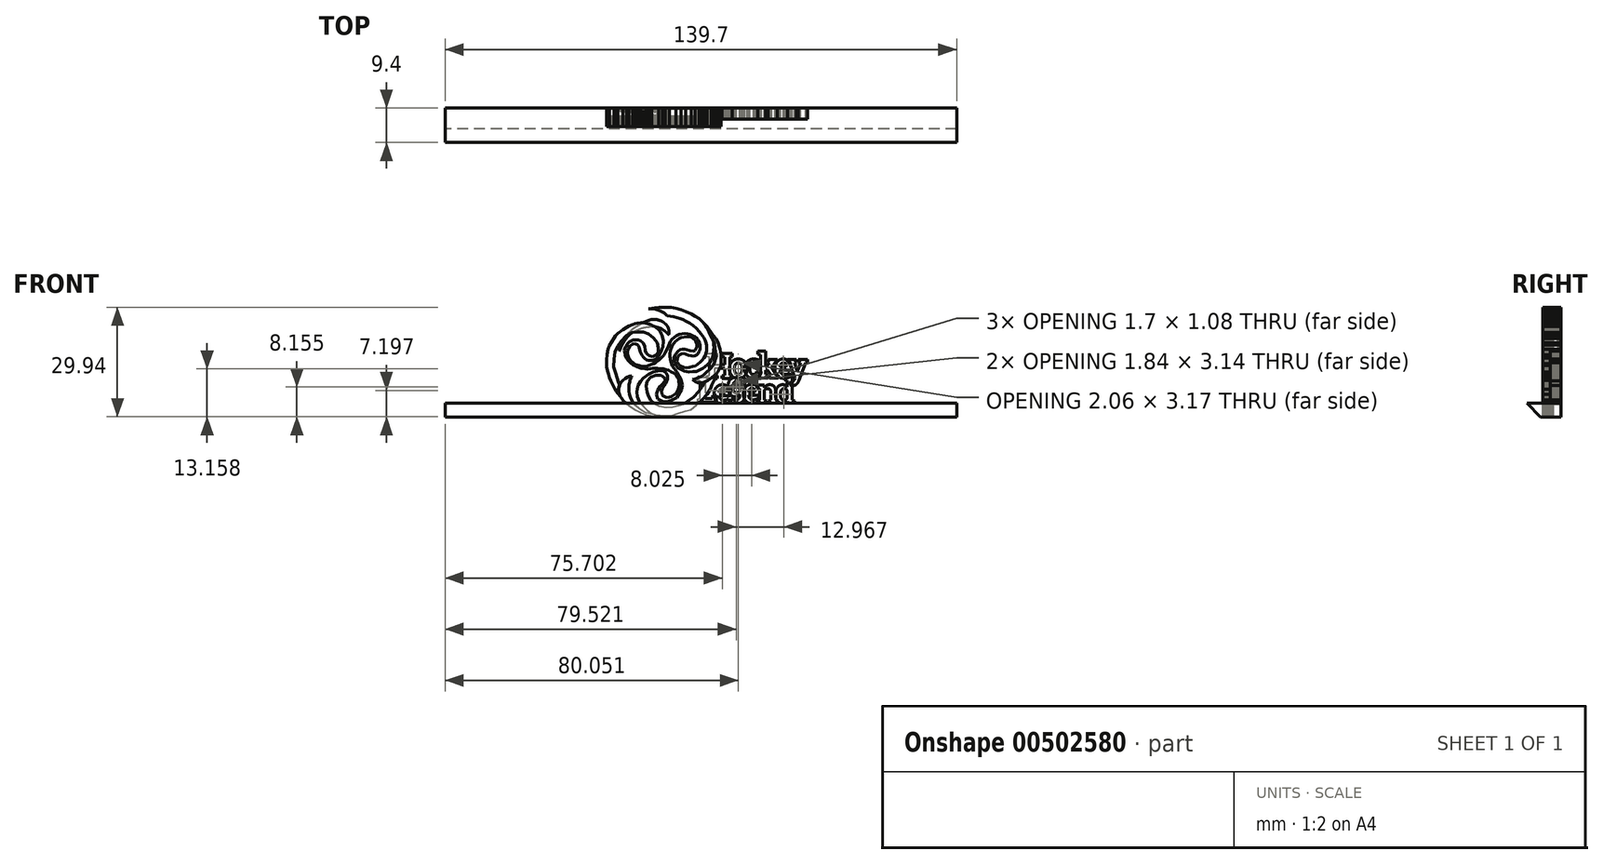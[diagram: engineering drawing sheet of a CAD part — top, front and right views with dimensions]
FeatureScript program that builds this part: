
annotation { "Feature Type Name" : "Feature", "Feature Type Description" : "" }
export const myFeature = defineFeature(function(context is Context, id is Id, definition is map)
    precondition{}
    {
        {
            var Q0;
            Q0=qCreatedBy(makeId("Front.planeOp"),FACE);
            var sketch = newSketch(context, id + "F0", { "sketchPlane" : qUnion([Q0])});
            skLineSegment(sketch, "E0", {"start": v(-33.7, 19.16) * mm, "end": v(-33.3, 20.48) * mm});
            skLineSegment(sketch, "E1", {"start": v(-33.3, 20.48) * mm, "end": v(-32.6, 22.47) * mm});
            skLineSegment(sketch, "E2", {"start": v(-32.6, 22.47) * mm, "end": v(-31.8, 23.73) * mm});
            skLineSegment(sketch, "E3", {"start": v(-31.8, 23.73) * mm, "end": v(-30.43, 25.5) * mm});
            skLineSegment(sketch, "E4", {"start": v(-30.43, 25.5) * mm, "end": v(-29.28, 26.69) * mm});
            skLineSegment(sketch, "E5", {"start": v(-29.28, 26.69) * mm, "end": v(-27.9, 27.7) * mm});
            skLineSegment(sketch, "E6", {"start": v(-27.9, 27.7) * mm, "end": v(-26.31, 28.61) * mm});
            skLineSegment(sketch, "E7", {"start": v(-26.31, 28.61) * mm, "end": v(-24.53, 29.36) * mm});
            skLineSegment(sketch, "E8", {"start": v(-24.53, 29.36) * mm, "end": v(-22.77, 30.03) * mm});
            skLineSegment(sketch, "E9", {"start": v(-20.78, 30.38) * mm, "end": v(-18.74, 30.57) * mm});
            skLineSegment(sketch, "E10", {"start": v(-18.74, 30.57) * mm, "end": v(-17.05, 30.57) * mm});
            skLineSegment(sketch, "E11", {"start": v(-17.05, 30.57) * mm, "end": v(-15.73, 30.37) * mm});
            skLineSegment(sketch, "E12", {"start": v(-15.73, 30.37) * mm, "end": v(-14.43, 30.08) * mm});
            skLineSegment(sketch, "E13", {"start": v(-14.43, 30.08) * mm, "end": v(-13.77, 29.88) * mm});
            skLineSegment(sketch, "E14", {"start": v(-13.77, 29.88) * mm, "end": v(-13.3, 29.7) * mm});
            skLineSegment(sketch, "E15", {"start": v(-13.3, 29.7) * mm, "end": v(-12.41, 29.39) * mm});
            skLineSegment(sketch, "E16", {"start": v(-12.41, 29.39) * mm, "end": v(-11.63, 29.01) * mm});
            skLineSegment(sketch, "E17", {"start": v(-11.63, 29.01) * mm, "end": v(-10.92, 28.65) * mm});
            skLineSegment(sketch, "E18", {"start": v(-10.92, 28.65) * mm, "end": v(-9.87, 28.07) * mm});
            skLineSegment(sketch, "E19", {"start": v(-9.87, 28.07) * mm, "end": v(-9.21, 27.61) * mm});
            skLineSegment(sketch, "E20", {"start": v(-9.21, 27.61) * mm, "end": v(-8.27, 26.91) * mm});
            skLineSegment(sketch, "E21", {"start": v(-8.27, 26.91) * mm, "end": v(-7.68, 26.29) * mm});
            skLineSegment(sketch, "E22", {"start": v(-7.68, 26.29) * mm, "end": v(-6.99, 25.65) * mm});
            skLineSegment(sketch, "E23", {"start": v(-6.99, 25.65) * mm, "end": v(-6.42, 25.01) * mm});
            skLineSegment(sketch, "E24", {"start": v(-6.42, 25.01) * mm, "end": v(-5.75, 24.03) * mm});
            skLineSegment(sketch, "E25", {"start": v(-5.75, 24.03) * mm, "end": v(-5.27, 23.32) * mm});
            skLineSegment(sketch, "E26", {"start": v(-5.27, 23.32) * mm, "end": v(-4.81, 22.67) * mm});
            skLineSegment(sketch, "E27", {"start": v(-4.81, 22.67) * mm, "end": v(-4.32, 21.95) * mm});
            skLineSegment(sketch, "E28", {"start": v(-4.32, 21.95) * mm, "end": v(-3.97, 21.3) * mm});
            skLineSegment(sketch, "E29", {"start": v(-3.97, 21.3) * mm, "end": v(-3.66, 20.68) * mm});
            skLineSegment(sketch, "E30", {"start": v(-3.66, 20.68) * mm, "end": v(-3.37, 19.88) * mm});
            skLineSegment(sketch, "E31", {"start": v(-3.37, 19.88) * mm, "end": v(-3.16, 19.05) * mm});
            skLineSegment(sketch, "E32", {"start": v(-3.16, 19.05) * mm, "end": v(-3, 18.35) * mm});
            skLineSegment(sketch, "E33", {"start": v(-3, 18.35) * mm, "end": v(-2.85, 17.43) * mm});
            skLineSegment(sketch, "E34", {"start": v(-2.85, 17.43) * mm, "end": v(-2.78, 16.73) * mm});
            skLineSegment(sketch, "E35", {"start": v(-2.78, 16.73) * mm, "end": v(-2.78, 15.96) * mm});
            skLineSegment(sketch, "E36", {"start": v(-2.78, 15.96) * mm, "end": v(-2.78, 15.27) * mm});
            skLineSegment(sketch, "E37", {"start": v(-2.78, 15.27) * mm, "end": v(-2.97, 14.6) * mm});
            skLineSegment(sketch, "E38", {"start": v(-2.97, 14.6) * mm, "end": v(-3.1, 14.21) * mm});
            skLineSegment(sketch, "E39", {"start": v(-3.1, 14.21) * mm, "end": v(-3.35, 13.67) * mm});
            skLineSegment(sketch, "E40", {"start": v(-3.35, 13.67) * mm, "end": v(-3.6, 13.13) * mm});
            skLineSegment(sketch, "E41", {"start": v(-3.6, 13.13) * mm, "end": v(-3.8, 12.58) * mm});
            skLineSegment(sketch, "E42", {"start": v(-3.8, 12.58) * mm, "end": v(-4.04, 11.95) * mm});
            skLineSegment(sketch, "E43", {"start": v(-4.04, 11.95) * mm, "end": v(-4.27, 11.36) * mm});
            skLineSegment(sketch, "E44", {"start": v(-4.27, 11.36) * mm, "end": v(-4.6, 10.6) * mm});
            skLineSegment(sketch, "E45", {"start": v(-4.6, 10.6) * mm, "end": v(-4.94, 9.83) * mm});
            skLineSegment(sketch, "E46", {"start": v(-4.94, 9.83) * mm, "end": v(-5.28, 9.04) * mm});
            skLineSegment(sketch, "E47", {"start": v(-5.28, 9.04) * mm, "end": v(-5.57, 8.47) * mm});
            skLineSegment(sketch, "E48", {"start": v(-5.57, 8.47) * mm, "end": v(-5.92, 7.85) * mm});
            skLineSegment(sketch, "E49", {"start": v(-5.92, 7.85) * mm, "end": v(-6.38, 7.05) * mm});
            skLineSegment(sketch, "E50", {"start": v(-6.38, 7.05) * mm, "end": v(-6.91, 6.24) * mm});
            skLineSegment(sketch, "E51", {"start": v(-6.91, 6.24) * mm, "end": v(-7.44, 5.65) * mm});
            skLineSegment(sketch, "E52", {"start": v(-7.44, 5.65) * mm, "end": v(-8.07, 5) * mm});
            skLineSegment(sketch, "E53", {"start": v(-8.07, 5) * mm, "end": v(-8.73, 4.35) * mm});
            skLineSegment(sketch, "E54", {"start": v(-8.73, 4.35) * mm, "end": v(-9.42, 3.8) * mm});
            skLineSegment(sketch, "E55", {"start": v(-9.42, 3.8) * mm, "end": v(-10.18, 3.24) * mm});
            skLineSegment(sketch, "E56", {"start": v(-10.18, 3.24) * mm, "end": v(-10.97, 2.83) * mm});
            skLineSegment(sketch, "E57", {"start": v(-10.97, 2.83) * mm, "end": v(-11.64, 2.49) * mm});
            skLineSegment(sketch, "E58", {"start": v(-11.64, 2.49) * mm, "end": v(-12.63, 2.09) * mm});
            skLineSegment(sketch, "E59", {"start": v(-12.63, 2.09) * mm, "end": v(-13.64, 1.64) * mm});
            skLineSegment(sketch, "E60", {"start": v(-13.64, 1.64) * mm, "end": v(-14.42, 1.42) * mm});
            skLineSegment(sketch, "E61", {"start": v(-14.42, 1.42) * mm, "end": v(-15.36, 1.15) * mm});
            skLineSegment(sketch, "E62", {"start": v(-15.36, 1.15) * mm, "end": v(-16.56, 0.85) * mm});
            skLineSegment(sketch, "E63", {"start": v(-16.56, 0.85) * mm, "end": v(-17.54, 0.76) * mm});
            skLineSegment(sketch, "E64", {"start": v(-17.54, 0.76) * mm, "end": v(-19.06, 0.76) * mm});
            skLineSegment(sketch, "E65", {"start": v(-19.06, 0.76) * mm, "end": v(-20.61, 0.76) * mm});
            skLineSegment(sketch, "E66", {"start": v(-20.61, 0.76) * mm, "end": v(-21.52, 0.9) * mm});
            skLineSegment(sketch, "E67", {"start": v(-21.52, 0.9) * mm, "end": v(-22.42, 1) * mm});
            skLineSegment(sketch, "E68", {"start": v(-22.42, 1) * mm, "end": v(-23.55, 1.3) * mm});
            skLineSegment(sketch, "E69", {"start": v(-23.55, 1.3) * mm, "end": v(-24.7, 1.7) * mm});
            skLineSegment(sketch, "E70", {"start": v(-24.7, 1.7) * mm, "end": v(-25.68, 2.17) * mm});
            skLineSegment(sketch, "E71", {"start": v(-25.68, 2.17) * mm, "end": v(-26.8, 2.85) * mm});
            skLineSegment(sketch, "E72", {"start": v(-26.8, 2.85) * mm, "end": v(-27.8, 3.53) * mm});
            skLineSegment(sketch, "E73", {"start": v(-27.8, 3.53) * mm, "end": v(-28.58, 4.16) * mm});
            skLineSegment(sketch, "E74", {"start": v(-28.58, 4.16) * mm, "end": v(-29.23, 4.73) * mm});
            skLineSegment(sketch, "E75", {"start": v(-29.23, 4.73) * mm, "end": v(-29.99, 5.52) * mm});
            skLineSegment(sketch, "E76", {"start": v(-29.99, 5.52) * mm, "end": v(-30.66, 6.36) * mm});
            skLineSegment(sketch, "E77", {"start": v(-30.66, 6.36) * mm, "end": v(-31.17, 7.15) * mm});
            skLineSegment(sketch, "E78", {"start": v(-31.17, 7.15) * mm, "end": v(-31.73, 7.95) * mm});
            skLineSegment(sketch, "E79", {"start": v(-31.73, 7.95) * mm, "end": v(-32.2, 8.8) * mm});
            skLineSegment(sketch, "E80", {"start": v(-32.2, 8.8) * mm, "end": v(-32.59, 9.61) * mm});
            skLineSegment(sketch, "E81", {"start": v(-32.59, 9.61) * mm, "end": v(-33.05, 10.63) * mm});
            skLineSegment(sketch, "E82", {"start": v(-33.05, 10.63) * mm, "end": v(-33.36, 11.4) * mm});
            skLineSegment(sketch, "E83", {"start": v(-33.36, 11.4) * mm, "end": v(-33.53, 11.9) * mm});
            skLineSegment(sketch, "E84", {"start": v(-33.53, 11.9) * mm, "end": v(-33.7, 12.5) * mm});
            skLineSegment(sketch, "E85", {"start": v(-33.7, 12.5) * mm, "end": v(-33.89, 13.2) * mm});
            skLineSegment(sketch, "E86", {"start": v(-33.89, 13.2) * mm, "end": v(-34.04, 14.07) * mm});
            skLineSegment(sketch, "E87", {"start": v(-34.04, 14.07) * mm, "end": v(-34.09, 14.6) * mm});
            skLineSegment(sketch, "E88", {"start": v(-34.09, 14.6) * mm, "end": v(-34.17, 15.53) * mm});
            skLineSegment(sketch, "E89", {"start": v(-34.17, 15.53) * mm, "end": v(-34.17, 16.35) * mm});
            skLineSegment(sketch, "E90", {"start": v(-34.17, 16.35) * mm, "end": v(-34.1, 17.06) * mm});
            skLineSegment(sketch, "E91", {"start": v(-34.1, 17.06) * mm, "end": v(-33.97, 17.72) * mm});
            skLineSegment(sketch, "E92", {"start": v(-33.97, 17.72) * mm, "end": v(-33.9, 18.17) * mm});
            skLineSegment(sketch, "E93", {"start": v(-33.9, 18.17) * mm, "end": v(-33.7, 19.16) * mm});
            skLineSegment(sketch, "E94", {"start": v(-33.7, 19.16) * mm, "end": v(-32.8, 21.26) * mm});
            skLineSegment(sketch, "E95", {"start": v(-32.8, 21.26) * mm, "end": v(-31.7, 23.03) * mm});
            skLineSegment(sketch, "E96", {"start": v(-31.7, 23.03) * mm, "end": v(-30.69, 24.35) * mm});
            skLineSegment(sketch, "E97", {"start": v(-30.69, 24.35) * mm, "end": v(-29.56, 25.32) * mm});
            skLineSegment(sketch, "E98", {"start": v(-29.56, 25.32) * mm, "end": v(-28.24, 26.19) * mm});
            skLineSegment(sketch, "E99", {"start": v(-28.24, 26.19) * mm, "end": v(-26, 27.12) * mm});
            skLineSegment(sketch, "E100", {"start": v(-26, 27.12) * mm, "end": v(-24.15, 27.5) * mm});
            skLineSegment(sketch, "E101", {"start": v(-24.15, 27.5) * mm, "end": v(-22.35, 27.66) * mm});
            skLineSegment(sketch, "E102", {"start": v(-22.35, 27.66) * mm, "end": v(-20.72, 27.34) * mm});
            skLineSegment(sketch, "E103", {"start": v(-20.72, 27.34) * mm, "end": v(-19.5, 26.97) * mm});
            skLineSegment(sketch, "E104", {"start": v(-19.5, 26.97) * mm, "end": v(-18.35, 26.19) * mm});
            skLineSegment(sketch, "E105", {"start": v(-18.35, 26.19) * mm, "end": v(-17.54, 25.56) * mm});
            skLineSegment(sketch, "E106", {"start": v(-17.54, 25.56) * mm, "end": v(-16.86, 24.84) * mm});
            skLineSegment(sketch, "E107", {"start": v(-16.86, 24.84) * mm, "end": v(-16.7, 25.66) * mm});
            skLineSegment(sketch, "E108", {"start": v(-16.7, 25.66) * mm, "end": v(-16.76, 26.4) * mm});
            skLineSegment(sketch, "E109", {"start": v(-16.76, 26.4) * mm, "end": v(-17, 27.17) * mm});
            skLineSegment(sketch, "E110", {"start": v(-17, 27.17) * mm, "end": v(-17.38, 27.85) * mm});
            skLineSegment(sketch, "E111", {"start": v(-17.38, 27.85) * mm, "end": v(-17.54, 28.14) * mm});
            skLineSegment(sketch, "E112", {"start": v(-17.54, 28.14) * mm, "end": v(-18.13, 28.65) * mm});
            skLineSegment(sketch, "E113", {"start": v(-18.13, 28.65) * mm, "end": v(-18.74, 29.18) * mm});
            skLineSegment(sketch, "E114", {"start": v(-18.74, 29.18) * mm, "end": v(-19.33, 29.5) * mm});
            skLineSegment(sketch, "E115", {"start": v(-19.33, 29.5) * mm, "end": v(-20.06, 29.73) * mm});
            skLineSegment(sketch, "E116", {"start": v(-20.06, 29.73) * mm, "end": v(-20.78, 29.94) * mm});
            skLineSegment(sketch, "E117", {"start": v(-20.78, 29.94) * mm, "end": v(-21.32, 30.05) * mm});
            skLineSegment(sketch, "E118", {"start": v(-21.32, 30.05) * mm, "end": v(-21.83, 30.05) * mm});
            skLineSegment(sketch, "E119", {"start": v(-21.83, 30.05) * mm, "end": v(-22.48, 30) * mm});
            skLineSegment(sketch, "E120", {"start": v(-22.48, 30) * mm, "end": v(-22.77, 30.03) * mm});
            skSolve(sketch);
        }
        {
            var Q0;
            Q0=qCreatedBy(makeId("Front.planeOp"),FACE);
            var sketch = newSketch(context, id + "F1", { "sketchPlane" : qUnion([Q0])});
            skLineSegment(sketch, "E121", {"start": v(-17.59, 28.18) * mm, "end": v(-16.68, 28.05) * mm});
            skLineSegment(sketch, "E122", {"start": v(-16.68, 28.05) * mm, "end": v(-15.74, 27.89) * mm});
            skLineSegment(sketch, "E123", {"start": v(-15.74, 27.89) * mm, "end": v(-14.88, 27.66) * mm});
            skLineSegment(sketch, "E124", {"start": v(-14.88, 27.66) * mm, "end": v(-14, 27.4) * mm});
            skLineSegment(sketch, "E125", {"start": v(-14, 27.4) * mm, "end": v(-13.3, 27.13) * mm});
            skLineSegment(sketch, "E126", {"start": v(-13.3, 27.13) * mm, "end": v(-12.35, 26.65) * mm});
            skLineSegment(sketch, "E127", {"start": v(-12.35, 26.65) * mm, "end": v(-11.37, 26.16) * mm});
            skLineSegment(sketch, "E128", {"start": v(-11.37, 26.16) * mm, "end": v(-10.4, 25.46) * mm});
            skLineSegment(sketch, "E129", {"start": v(-10.4, 25.46) * mm, "end": v(-9.57, 24.7) * mm});
            skLineSegment(sketch, "E130", {"start": v(-9.57, 24.7) * mm, "end": v(-8.82, 23.91) * mm});
            skLineSegment(sketch, "E131", {"start": v(-8.82, 23.91) * mm, "end": v(-8.25, 23.18) * mm});
            skLineSegment(sketch, "E132", {"start": v(-8.25, 23.18) * mm, "end": v(-7.58, 22.23) * mm});
            skLineSegment(sketch, "E133", {"start": v(-7.58, 22.23) * mm, "end": v(-7.2, 21.49) * mm});
            skLineSegment(sketch, "E134", {"start": v(-7.2, 21.49) * mm, "end": v(-6.86, 20.66) * mm});
            skLineSegment(sketch, "E135", {"start": v(-6.86, 20.66) * mm, "end": v(-6.73, 20.08) * mm});
            skLineSegment(sketch, "E136", {"start": v(-6.73, 20.08) * mm, "end": v(-6.73, 19.2) * mm});
            skLineSegment(sketch, "E137", {"start": v(-6.73, 19.2) * mm, "end": v(-6.78, 18.56) * mm});
            skLineSegment(sketch, "E138", {"start": v(-6.78, 18.56) * mm, "end": v(-6.98, 17.79) * mm});
            skLineSegment(sketch, "E139", {"start": v(-6.98, 17.79) * mm, "end": v(-7.2, 17.29) * mm});
            skLineSegment(sketch, "E140", {"start": v(-7.2, 17.29) * mm, "end": v(-7.52, 16.69) * mm});
            skLineSegment(sketch, "E141", {"start": v(-7.52, 16.69) * mm, "end": v(-8.02, 16.03) * mm});
            skLineSegment(sketch, "E142", {"start": v(-8.02, 16.03) * mm, "end": v(-8.55, 15.5) * mm});
            skLineSegment(sketch, "E143", {"start": v(-8.55, 15.5) * mm, "end": v(-9.17, 15.02) * mm});
            skLineSegment(sketch, "E144", {"start": v(-9.17, 15.02) * mm, "end": v(-9.81, 14.52) * mm});
            skLineSegment(sketch, "E145", {"start": v(-9.81, 14.52) * mm, "end": v(-10.54, 14.3) * mm});
            skLineSegment(sketch, "E146", {"start": v(-10.54, 14.3) * mm, "end": v(-11.44, 14.1) * mm});
            skLineSegment(sketch, "E147", {"start": v(-11.44, 14.1) * mm, "end": v(-12.2, 14) * mm});
            skLineSegment(sketch, "E148", {"start": v(-12.2, 14) * mm, "end": v(-13.06, 14.14) * mm});
            skLineSegment(sketch, "E149", {"start": v(-13.06, 14.14) * mm, "end": v(-13.88, 14.47) * mm});
            skLineSegment(sketch, "E150", {"start": v(-13.88, 14.47) * mm, "end": v(-14.41, 14.82) * mm});
            skLineSegment(sketch, "E151", {"start": v(-14.41, 14.82) * mm, "end": v(-14.66, 15.3) * mm});
            skLineSegment(sketch, "E152", {"start": v(-14.66, 15.3) * mm, "end": v(-14.86, 15.77) * mm});
            skLineSegment(sketch, "E153", {"start": v(-14.86, 15.77) * mm, "end": v(-14.8, 16.39) * mm});
            skLineSegment(sketch, "E154", {"start": v(-14.8, 16.39) * mm, "end": v(-14.65, 16.95) * mm});
            skLineSegment(sketch, "E155", {"start": v(-14.65, 16.95) * mm, "end": v(-14.14, 17.46) * mm});
            skLineSegment(sketch, "E156", {"start": v(-14.14, 17.46) * mm, "end": v(-13.66, 17.71) * mm});
            skLineSegment(sketch, "E157", {"start": v(-13.66, 17.71) * mm, "end": v(-13.04, 17.85) * mm});
            skLineSegment(sketch, "E158", {"start": v(-13.04, 17.85) * mm, "end": v(-12.42, 17.7) * mm});
            skLineSegment(sketch, "E159", {"start": v(-12.42, 17.7) * mm, "end": v(-11.69, 17.43) * mm});
            skLineSegment(sketch, "E160", {"start": v(-11.69, 17.43) * mm, "end": v(-11.01, 17.26) * mm});
            skLineSegment(sketch, "E161", {"start": v(-11.01, 17.26) * mm, "end": v(-10.44, 17.19) * mm});
            skLineSegment(sketch, "E162", {"start": v(-10.44, 17.19) * mm, "end": v(-10, 17.28) * mm});
            skLineSegment(sketch, "E163", {"start": v(-10, 17.28) * mm, "end": v(-9.5, 17.54) * mm});
            skLineSegment(sketch, "E164", {"start": v(-9.5, 17.54) * mm, "end": v(-9.1, 17.86) * mm});
            skLineSegment(sketch, "E165", {"start": v(-9.1, 17.86) * mm, "end": v(-8.9, 18.3) * mm});
            skLineSegment(sketch, "E166", {"start": v(-8.9, 18.3) * mm, "end": v(-8.72, 18.67) * mm});
            skLineSegment(sketch, "E167", {"start": v(-8.72, 18.67) * mm, "end": v(-8.6, 19.14) * mm});
            skLineSegment(sketch, "E168", {"start": v(-8.6, 19.14) * mm, "end": v(-8.6, 19.54) * mm});
            skLineSegment(sketch, "E169", {"start": v(-8.6, 19.54) * mm, "end": v(-8.6, 20.08) * mm});
            skLineSegment(sketch, "E170", {"start": v(-8.6, 20.08) * mm, "end": v(-8.73, 20.69) * mm});
            skLineSegment(sketch, "E171", {"start": v(-8.73, 20.69) * mm, "end": v(-9, 21.33) * mm});
            skLineSegment(sketch, "E172", {"start": v(-9, 21.33) * mm, "end": v(-9.2, 21.7) * mm});
            skLineSegment(sketch, "E173", {"start": v(-9.2, 21.7) * mm, "end": v(-9.48, 22.06) * mm});
            skLineSegment(sketch, "E174", {"start": v(-9.48, 22.06) * mm, "end": v(-9.97, 22.5) * mm});
            skLineSegment(sketch, "E175", {"start": v(-9.97, 22.5) * mm, "end": v(-10.54, 22.77) * mm});
            skLineSegment(sketch, "E176", {"start": v(-10.54, 22.77) * mm, "end": v(-11.33, 23.08) * mm});
            skLineSegment(sketch, "E177", {"start": v(-11.33, 23.08) * mm, "end": v(-11.96, 23.25) * mm});
            skLineSegment(sketch, "E178", {"start": v(-11.96, 23.25) * mm, "end": v(-12.7, 23.32) * mm});
            skLineSegment(sketch, "E179", {"start": v(-12.7, 23.32) * mm, "end": v(-13.51, 23.23) * mm});
            skLineSegment(sketch, "E180", {"start": v(-13.51, 23.23) * mm, "end": v(-14.27, 23.08) * mm});
            skLineSegment(sketch, "E181", {"start": v(-14.27, 23.08) * mm, "end": v(-15.04, 22.67) * mm});
            skLineSegment(sketch, "E182", {"start": v(-15.04, 22.67) * mm, "end": v(-15.57, 22.26) * mm});
            skLineSegment(sketch, "E183", {"start": v(-15.57, 22.26) * mm, "end": v(-16.16, 21.8) * mm});
            skLineSegment(sketch, "E184", {"start": v(-16.16, 21.8) * mm, "end": v(-16.62, 21.17) * mm});
            skLineSegment(sketch, "E185", {"start": v(-16.62, 21.17) * mm, "end": v(-16.97, 20.58) * mm});
            skLineSegment(sketch, "E186", {"start": v(-16.97, 20.58) * mm, "end": v(-17.24, 19.87) * mm});
            skLineSegment(sketch, "E187", {"start": v(-17.24, 19.87) * mm, "end": v(-17.63, 19.02) * mm});
            skLineSegment(sketch, "E188", {"start": v(-17.63, 19.02) * mm, "end": v(-18.02, 18.18) * mm});
            skLineSegment(sketch, "E189", {"start": v(-18.02, 18.18) * mm, "end": v(-18.47, 17.4) * mm});
            skLineSegment(sketch, "E190", {"start": v(-18.47, 17.4) * mm, "end": v(-19.07, 16.73) * mm});
            skLineSegment(sketch, "E191", {"start": v(-19.07, 16.73) * mm, "end": v(-19.8, 16.05) * mm});
            skLineSegment(sketch, "E192", {"start": v(-19.8, 16.05) * mm, "end": v(-20.62, 15.5) * mm});
            skLineSegment(sketch, "E193", {"start": v(-20.62, 15.5) * mm, "end": v(-21.3, 15.14) * mm});
            skLineSegment(sketch, "E194", {"start": v(-21.3, 15.14) * mm, "end": v(-22.02, 14.87) * mm});
            skLineSegment(sketch, "E195", {"start": v(-22.02, 14.87) * mm, "end": v(-22.85, 14.53) * mm});
            skLineSegment(sketch, "E196", {"start": v(-22.85, 14.53) * mm, "end": v(-23.59, 14.38) * mm});
            skLineSegment(sketch, "E197", {"start": v(-23.59, 14.38) * mm, "end": v(-24.4, 14.38) * mm});
            skLineSegment(sketch, "E198", {"start": v(-24.4, 14.38) * mm, "end": v(-25.23, 14.53) * mm});
            skLineSegment(sketch, "E199", {"start": v(-25.23, 14.53) * mm, "end": v(-26.19, 14.9) * mm});
            skLineSegment(sketch, "E200", {"start": v(-26.19, 14.9) * mm, "end": v(-26.89, 15.3) * mm});
            skLineSegment(sketch, "E201", {"start": v(-26.89, 15.3) * mm, "end": v(-27.37, 15.75) * mm});
            skLineSegment(sketch, "E202", {"start": v(-27.37, 15.75) * mm, "end": v(-27.81, 16.32) * mm});
            skLineSegment(sketch, "E203", {"start": v(-27.81, 16.32) * mm, "end": v(-28.1, 16.87) * mm});
            skLineSegment(sketch, "E204", {"start": v(-28.1, 16.87) * mm, "end": v(-28.31, 17.7) * mm});
            skLineSegment(sketch, "E205", {"start": v(-28.31, 17.7) * mm, "end": v(-28.31, 18.37) * mm});
            skLineSegment(sketch, "E206", {"start": v(-28.31, 18.37) * mm, "end": v(-28.21, 18.94) * mm});
            skLineSegment(sketch, "E207", {"start": v(-28.21, 18.94) * mm, "end": v(-28.1, 19.34) * mm});
            skLineSegment(sketch, "E208", {"start": v(-28.1, 19.34) * mm, "end": v(-27.77, 19.9) * mm});
            skLineSegment(sketch, "E209", {"start": v(-27.77, 19.9) * mm, "end": v(-27.4, 20.24) * mm});
            skLineSegment(sketch, "E210", {"start": v(-27.4, 20.24) * mm, "end": v(-26.9, 20.48) * mm});
            skLineSegment(sketch, "E211", {"start": v(-26.9, 20.48) * mm, "end": v(-26.35, 20.53) * mm});
            skLineSegment(sketch, "E212", {"start": v(-26.35, 20.53) * mm, "end": v(-26.08, 20.47) * mm});
            skLineSegment(sketch, "E213", {"start": v(-26.08, 20.47) * mm, "end": v(-25.65, 20.3) * mm});
            skLineSegment(sketch, "E214", {"start": v(-25.65, 20.3) * mm, "end": v(-25.4, 20.02) * mm});
            skLineSegment(sketch, "E215", {"start": v(-25.4, 20.02) * mm, "end": v(-25.24, 19.53) * mm});
            skLineSegment(sketch, "E216", {"start": v(-25.24, 19.53) * mm, "end": v(-24.88, 18.41) * mm});
            skLineSegment(sketch, "E217", {"start": v(-24.88, 18.41) * mm, "end": v(-24.66, 17.85) * mm});
            skLineSegment(sketch, "E218", {"start": v(-24.66, 17.85) * mm, "end": v(-24.4, 17.37) * mm});
            skLineSegment(sketch, "E219", {"start": v(-24.4, 17.37) * mm, "end": v(-24.07, 16.93) * mm});
            skLineSegment(sketch, "E220", {"start": v(-24.07, 16.93) * mm, "end": v(-23.62, 16.44) * mm});
            skLineSegment(sketch, "E221", {"start": v(-23.62, 16.44) * mm, "end": v(-23.12, 16.15) * mm});
            skLineSegment(sketch, "E222", {"start": v(-23.12, 16.15) * mm, "end": v(-22.6, 16.01) * mm});
            skLineSegment(sketch, "E223", {"start": v(-22.6, 16.01) * mm, "end": v(-22.12, 15.93) * mm});
            skLineSegment(sketch, "E224", {"start": v(-22.12, 15.93) * mm, "end": v(-21.5, 16.01) * mm});
            skLineSegment(sketch, "E225", {"start": v(-21.5, 16.01) * mm, "end": v(-21.12, 16.12) * mm});
            skLineSegment(sketch, "E226", {"start": v(-21.12, 16.12) * mm, "end": v(-20.65, 16.37) * mm});
            skLineSegment(sketch, "E227", {"start": v(-20.65, 16.37) * mm, "end": v(-20.16, 16.83) * mm});
            skLineSegment(sketch, "E228", {"start": v(-20.16, 16.83) * mm, "end": v(-19.85, 17.1) * mm});
            skLineSegment(sketch, "E229", {"start": v(-19.85, 17.1) * mm, "end": v(-19.6, 17.6) * mm});
            skLineSegment(sketch, "E230", {"start": v(-19.6, 17.6) * mm, "end": v(-19.35, 18.1) * mm});
            skLineSegment(sketch, "E231", {"start": v(-19.35, 18.1) * mm, "end": v(-19.03, 18.64) * mm});
            skLineSegment(sketch, "E232", {"start": v(-19.03, 18.64) * mm, "end": v(-18.91, 19.23) * mm});
            skLineSegment(sketch, "E233", {"start": v(-18.91, 19.23) * mm, "end": v(-18.77, 19.65) * mm});
            skLineSegment(sketch, "E234", {"start": v(-18.77, 19.65) * mm, "end": v(-18.67, 20.1) * mm});
            skLineSegment(sketch, "E235", {"start": v(-18.67, 20.1) * mm, "end": v(-18.62, 20.77) * mm});
            skLineSegment(sketch, "E236", {"start": v(-18.62, 20.77) * mm, "end": v(-18.62, 21.3) * mm});
            skLineSegment(sketch, "E237", {"start": v(-18.62, 21.3) * mm, "end": v(-18.68, 21.91) * mm});
            skLineSegment(sketch, "E238", {"start": v(-18.68, 21.91) * mm, "end": v(-18.97, 22.9) * mm});
            skLineSegment(sketch, "E239", {"start": v(-18.97, 22.9) * mm, "end": v(-19.2, 23.37) * mm});
            skLineSegment(sketch, "E240", {"start": v(-19.2, 23.37) * mm, "end": v(-19.4, 23.74) * mm});
            skLineSegment(sketch, "E241", {"start": v(-19.4, 23.74) * mm, "end": v(-19.88, 24.36) * mm});
            skLineSegment(sketch, "E242", {"start": v(-19.88, 24.36) * mm, "end": v(-20.56, 24.97) * mm});
            skLineSegment(sketch, "E243", {"start": v(-20.56, 24.97) * mm, "end": v(-21.04, 25.24) * mm});
            skLineSegment(sketch, "E244", {"start": v(-21.04, 25.24) * mm, "end": v(-21.38, 25.44) * mm});
            skLineSegment(sketch, "E245", {"start": v(-21.38, 25.44) * mm, "end": v(-22.12, 25.85) * mm});
            skLineSegment(sketch, "E246", {"start": v(-22.12, 25.85) * mm, "end": v(-22.57, 25.95) * mm});
            skLineSegment(sketch, "E247", {"start": v(-22.57, 25.95) * mm, "end": v(-23.45, 26.18) * mm});
            skLineSegment(sketch, "E248", {"start": v(-23.45, 26.18) * mm, "end": v(-24.1, 26.3) * mm});
            skLineSegment(sketch, "E249", {"start": v(-24.1, 26.3) * mm, "end": v(-24.77, 26.26) * mm});
            skLineSegment(sketch, "E250", {"start": v(-24.77, 26.26) * mm, "end": v(-25.66, 26.17) * mm});
            skLineSegment(sketch, "E251", {"start": v(-25.66, 26.17) * mm, "end": v(-26.27, 25.98) * mm});
            skLineSegment(sketch, "E252", {"start": v(-26.27, 25.98) * mm, "end": v(-26.98, 25.74) * mm});
            skLineSegment(sketch, "E253", {"start": v(-26.98, 25.74) * mm, "end": v(-27.95, 25.34) * mm});
            skLineSegment(sketch, "E254", {"start": v(-27.95, 25.34) * mm, "end": v(-28.58, 25.07) * mm});
            skLineSegment(sketch, "E255", {"start": v(-28.58, 25.07) * mm, "end": v(-29.6, 24.43) * mm});
            skLineSegment(sketch, "E256", {"start": v(-29.6, 24.43) * mm, "end": v(-30.3, 23.9) * mm});
            skLineSegment(sketch, "E257", {"start": v(-30.3, 23.9) * mm, "end": v(-31.05, 23.3) * mm});
            skLineSegment(sketch, "E258", {"start": v(-31.05, 23.3) * mm, "end": v(-31.6, 22.7) * mm});
            skLineSegment(sketch, "E259", {"start": v(-31.6, 22.7) * mm, "end": v(-32.06, 22.14) * mm});
            skLineSegment(sketch, "E260", {"start": v(-32.06, 22.14) * mm, "end": v(-33.26, 20.08) * mm});
            skLineSegment(sketch, "E261", {"start": v(-33.26, 20.08) * mm, "end": v(-33.7, 19.08) * mm});
            skLineSegment(sketch, "E262", {"start": v(-33.7, 19.08) * mm, "end": v(-33.95, 17.68) * mm});
            skLineSegment(sketch, "E263", {"start": v(-33.95, 17.68) * mm, "end": v(-34.13, 16.12) * mm});
            skLineSegment(sketch, "E264", {"start": v(-34.13, 16.12) * mm, "end": v(-34.13, 15.34) * mm});
            skLineSegment(sketch, "E265", {"start": v(-34.13, 15.34) * mm, "end": v(-34.04, 14.24) * mm});
            skLineSegment(sketch, "E266", {"start": v(-34.04, 14.24) * mm, "end": v(-33.83, 13.12) * mm});
            skLineSegment(sketch, "E267", {"start": v(-33.83, 13.12) * mm, "end": v(-33.6, 12.35) * mm});
            skLineSegment(sketch, "E268", {"start": v(-33.6, 12.35) * mm, "end": v(-33.3, 11.34) * mm});
            skLineSegment(sketch, "E269", {"start": v(-33.3, 11.34) * mm, "end": v(-32.93, 10.45) * mm});
            skLineSegment(sketch, "E270", {"start": v(-32.93, 10.45) * mm, "end": v(-32.6, 9.62) * mm});
            skLineSegment(sketch, "E271", {"start": v(-32.6, 9.62) * mm, "end": v(-32.3, 9.05) * mm});
            skLineSegment(sketch, "E272", {"start": v(-32.3, 9.05) * mm, "end": v(-31.54, 7.63) * mm});
            skLineSegment(sketch, "E273", {"start": v(-31.54, 7.63) * mm, "end": v(-30.98, 6.91) * mm});
            skLineSegment(sketch, "E274", {"start": v(-30.98, 6.91) * mm, "end": v(-30.4, 6.16) * mm});
            skLineSegment(sketch, "E275", {"start": v(-30.4, 6.16) * mm, "end": v(-30.82, 7.32) * mm});
            skLineSegment(sketch, "E276", {"start": v(-30.82, 7.32) * mm, "end": v(-30.82, 8.38) * mm});
            skLineSegment(sketch, "E277", {"start": v(-30.82, 8.38) * mm, "end": v(-30.56, 9.17) * mm});
            skLineSegment(sketch, "E278", {"start": v(-30.56, 9.17) * mm, "end": v(-30.96, 10.11) * mm});
            skLineSegment(sketch, "E279", {"start": v(-30.96, 10.11) * mm, "end": v(-31.54, 12.36) * mm});
            skLineSegment(sketch, "E280", {"start": v(-31.54, 12.36) * mm, "end": v(-32.14, 14.24) * mm});
            skLineSegment(sketch, "E281", {"start": v(-32.14, 14.24) * mm, "end": v(-32.1, 16.32) * mm});
            skLineSegment(sketch, "E282", {"start": v(-32.1, 16.32) * mm, "end": v(-31.74, 18.22) * mm});
            skLineSegment(sketch, "E283", {"start": v(-31.74, 18.22) * mm, "end": v(-30.97, 19.9) * mm});
            skLineSegment(sketch, "E284", {"start": v(-30.97, 19.9) * mm, "end": v(-30.14, 21.16) * mm});
            skLineSegment(sketch, "E285", {"start": v(-30.14, 21.16) * mm, "end": v(-28.8, 22.68) * mm});
            skLineSegment(sketch, "E286", {"start": v(-28.8, 22.68) * mm, "end": v(-27.04, 23.61) * mm});
            skLineSegment(sketch, "E287", {"start": v(-27.04, 23.61) * mm, "end": v(-25.72, 23.77) * mm});
            skLineSegment(sketch, "E288", {"start": v(-25.72, 23.77) * mm, "end": v(-23.98, 23.74) * mm});
            skLineSegment(sketch, "E289", {"start": v(-23.98, 23.74) * mm, "end": v(-22.6, 23.24) * mm});
            skLineSegment(sketch, "E290", {"start": v(-22.6, 23.24) * mm, "end": v(-21.28, 22.09) * mm});
            skLineSegment(sketch, "E291", {"start": v(-21.28, 22.09) * mm, "end": v(-20.24, 20.84) * mm});
            skLineSegment(sketch, "E292", {"start": v(-20.24, 20.84) * mm, "end": v(-19.95, 19.4) * mm});
            skLineSegment(sketch, "E293", {"start": v(-19.95, 19.4) * mm, "end": v(-20, 18.33) * mm});
            skLineSegment(sketch, "E294", {"start": v(-20, 18.33) * mm, "end": v(-20.5, 17.46) * mm});
            skLineSegment(sketch, "E295", {"start": v(-20.5, 17.46) * mm, "end": v(-21.55, 17.02) * mm});
            skLineSegment(sketch, "E296", {"start": v(-23.33, 18) * mm, "end": v(-23.54, 18.65) * mm});
            skLineSegment(sketch, "E297", {"start": v(-23.54, 18.65) * mm, "end": v(-23.67, 19.87) * mm});
            skLineSegment(sketch, "E298", {"start": v(-23.67, 19.87) * mm, "end": v(-24.2, 20.77) * mm});
            skLineSegment(sketch, "E299", {"start": v(-24.2, 20.77) * mm, "end": v(-24.84, 21.36) * mm});
            skLineSegment(sketch, "E300", {"start": v(-24.84, 21.36) * mm, "end": v(-25.5, 21.58) * mm});
            skLineSegment(sketch, "E301", {"start": v(-25.5, 21.58) * mm, "end": v(-26.81, 21.58) * mm});
            skLineSegment(sketch, "E302", {"start": v(-26.81, 21.58) * mm, "end": v(-27.81, 21.05) * mm});
            skLineSegment(sketch, "E303", {"start": v(-27.81, 21.05) * mm, "end": v(-28.43, 20.6) * mm});
            skLineSegment(sketch, "E304", {"start": v(-28.43, 20.6) * mm, "end": v(-28.92, 19.86) * mm});
            skLineSegment(sketch, "E305", {"start": v(-28.92, 19.86) * mm, "end": v(-29.16, 19.25) * mm});
            skLineSegment(sketch, "E306", {"start": v(-29.16, 19.25) * mm, "end": v(-29.2, 18.6) * mm});
            skLineSegment(sketch, "E307", {"start": v(-29.2, 18.6) * mm, "end": v(-29.05, 17.77) * mm});
            skLineSegment(sketch, "E308", {"start": v(-29.05, 17.77) * mm, "end": v(-28.96, 17.26) * mm});
            skLineSegment(sketch, "E309", {"start": v(-28.96, 17.26) * mm, "end": v(-28.6, 16.5) * mm});
            skLineSegment(sketch, "E310", {"start": v(-28.6, 16.5) * mm, "end": v(-28.12, 15.82) * mm});
            skLineSegment(sketch, "E311", {"start": v(-28.12, 15.82) * mm, "end": v(-27.66, 15.3) * mm});
            skLineSegment(sketch, "E312", {"start": v(-27.66, 15.3) * mm, "end": v(-26.86, 14.78) * mm});
            skLineSegment(sketch, "E313", {"start": v(-26.86, 14.78) * mm, "end": v(-26.24, 14.45) * mm});
            skLineSegment(sketch, "E314", {"start": v(-26.24, 14.45) * mm, "end": v(-25.65, 14.22) * mm});
            skLineSegment(sketch, "E315", {"start": v(-25.65, 14.22) * mm, "end": v(-24.73, 13.86) * mm});
            skLineSegment(sketch, "E316", {"start": v(-24.73, 13.86) * mm, "end": v(-23.5, 13.7) * mm});
            skLineSegment(sketch, "E317", {"start": v(-23.5, 13.7) * mm, "end": v(-22.86, 13.62) * mm});
            skLineSegment(sketch, "E318", {"start": v(-22.86, 13.62) * mm, "end": v(-22.18, 13.7) * mm});
            skLineSegment(sketch, "E319", {"start": v(-22.18, 13.7) * mm, "end": v(-21.5, 13.78) * mm});
            skLineSegment(sketch, "E320", {"start": v(-21.5, 13.78) * mm, "end": v(-21, 13.84) * mm});
            skLineSegment(sketch, "E321", {"start": v(-21, 13.84) * mm, "end": v(-20.09, 13.78) * mm});
            skLineSegment(sketch, "E322", {"start": v(-20.09, 13.78) * mm, "end": v(-19.35, 13.74) * mm});
            skLineSegment(sketch, "E323", {"start": v(-19.35, 13.74) * mm, "end": v(-18.6, 13.67) * mm});
            skLineSegment(sketch, "E324", {"start": v(-18.6, 13.67) * mm, "end": v(-17.87, 13.46) * mm});
            skLineSegment(sketch, "E325", {"start": v(-17.87, 13.46) * mm, "end": v(-17.18, 13.26) * mm});
            skLineSegment(sketch, "E326", {"start": v(-17.18, 13.26) * mm, "end": v(-16.4, 12.82) * mm});
            skLineSegment(sketch, "E327", {"start": v(-16.4, 12.82) * mm, "end": v(-15.76, 12.5) * mm});
            skLineSegment(sketch, "E328", {"start": v(-15.76, 12.5) * mm, "end": v(-15.1, 12.02) * mm});
            skLineSegment(sketch, "E329", {"start": v(-15.1, 12.02) * mm, "end": v(-14.75, 11.35) * mm});
            skLineSegment(sketch, "E330", {"start": v(-14.75, 11.35) * mm, "end": v(-14.46, 10.8) * mm});
            skLineSegment(sketch, "E331", {"start": v(-14.46, 10.8) * mm, "end": v(-14.36, 10.11) * mm});
            skLineSegment(sketch, "E332", {"start": v(-14.36, 10.11) * mm, "end": v(-14.32, 9.62) * mm});
            skLineSegment(sketch, "E333", {"start": v(-14.32, 9.62) * mm, "end": v(-14.33, 9.1) * mm});
            skLineSegment(sketch, "E334", {"start": v(-14.33, 9.1) * mm, "end": v(-14.41, 8.57) * mm});
            skLineSegment(sketch, "E335", {"start": v(-14.41, 8.57) * mm, "end": v(-14.55, 8.18) * mm});
            skLineSegment(sketch, "E336", {"start": v(-14.55, 8.18) * mm, "end": v(-14.76, 7.63) * mm});
            skLineSegment(sketch, "E337", {"start": v(-14.76, 7.63) * mm, "end": v(-14.91, 7.37) * mm});
            skLineSegment(sketch, "E338", {"start": v(-14.91, 7.37) * mm, "end": v(-15.27, 6.9) * mm});
            skLineSegment(sketch, "E339", {"start": v(-15.27, 6.9) * mm, "end": v(-15.72, 6.54) * mm});
            skLineSegment(sketch, "E340", {"start": v(-15.72, 6.54) * mm, "end": v(-16.37, 6.11) * mm});
            skLineSegment(sketch, "E341", {"start": v(-16.37, 6.11) * mm, "end": v(-16.98, 5.96) * mm});
            skLineSegment(sketch, "E342", {"start": v(-16.98, 5.96) * mm, "end": v(-17.46, 5.89) * mm});
            skLineSegment(sketch, "E343", {"start": v(-17.46, 5.89) * mm, "end": v(-18, 5.98) * mm});
            skLineSegment(sketch, "E344", {"start": v(-18, 5.98) * mm, "end": v(-18, 5.98) * mm});
            skLineSegment(sketch, "E345", {"start": v(-18, 5.98) * mm, "end": v(-18.68, 6.36) * mm});
            skLineSegment(sketch, "E346", {"start": v(-18.68, 6.36) * mm, "end": v(-19, 6.7) * mm});
            skLineSegment(sketch, "E347", {"start": v(-19, 6.7) * mm, "end": v(-19.08, 7.3) * mm});
            skLineSegment(sketch, "E348", {"start": v(-19.08, 7.3) * mm, "end": v(-19.13, 7.63) * mm});
            skLineSegment(sketch, "E349", {"start": v(-19.13, 7.63) * mm, "end": v(-18.85, 8.36) * mm});
            skLineSegment(sketch, "E350", {"start": v(-18.85, 8.36) * mm, "end": v(-18, 9.58) * mm});
            skLineSegment(sketch, "E351", {"start": v(-18, 9.58) * mm, "end": v(-18, 9.6) * mm});
            skLineSegment(sketch, "E352", {"start": v(-18, 9.6) * mm, "end": v(-17.5, 10.86) * mm});
            skLineSegment(sketch, "E353", {"start": v(-17.5, 10.86) * mm, "end": v(-17.47, 11.77) * mm});
            skLineSegment(sketch, "E354", {"start": v(-17.47, 11.77) * mm, "end": v(-17.82, 12.62) * mm});
            skLineSegment(sketch, "E355", {"start": v(-17.82, 12.62) * mm, "end": v(-18.76, 13.15) * mm});
            skLineSegment(sketch, "E356", {"start": v(-18.76, 13.15) * mm, "end": v(-20.27, 13.05) * mm});
            skLineSegment(sketch, "E357", {"start": v(-20.27, 13.05) * mm, "end": v(-21.36, 12.86) * mm});
            skLineSegment(sketch, "E358", {"start": v(-21.36, 12.86) * mm, "end": v(-22.64, 12.24) * mm});
            skLineSegment(sketch, "E359", {"start": v(-22.64, 12.24) * mm, "end": v(-24.04, 11.21) * mm});
            skLineSegment(sketch, "E360", {"start": v(-24.04, 11.21) * mm, "end": v(-24.86, 10.31) * mm});
            skLineSegment(sketch, "E361", {"start": v(-24.86, 10.31) * mm, "end": v(-25.41, 9.2) * mm});
            skLineSegment(sketch, "E362", {"start": v(-25.41, 9.2) * mm, "end": v(-25.66, 8.25) * mm});
            skLineSegment(sketch, "E363", {"start": v(-25.66, 8.25) * mm, "end": v(-25.8, 7.3) * mm});
            skLineSegment(sketch, "E364", {"start": v(-25.8, 7.3) * mm, "end": v(-25.73, 6.09) * mm});
            skLineSegment(sketch, "E365", {"start": v(-25.73, 6.09) * mm, "end": v(-25.16, 4.78) * mm});
            skLineSegment(sketch, "E366", {"start": v(-25.16, 4.78) * mm, "end": v(-24.07, 3.4) * mm});
            skLineSegment(sketch, "E367", {"start": v(-24.07, 3.4) * mm, "end": v(-23.05, 2.4) * mm});
            skLineSegment(sketch, "E368", {"start": v(-23.05, 2.4) * mm, "end": v(-21.87, 1.52) * mm});
            skLineSegment(sketch, "E369", {"start": v(-21.87, 1.52) * mm, "end": v(-20.68, 1.14) * mm});
            skLineSegment(sketch, "E370", {"start": v(-20.68, 1.14) * mm, "end": v(-19.55, 0.9) * mm});
            skLineSegment(sketch, "E371", {"start": v(-19.55, 0.9) * mm, "end": v(-18.27, 0.83) * mm});
            skLineSegment(sketch, "E372", {"start": v(-18.27, 0.83) * mm, "end": v(-16.45, 0.9) * mm});
            skLineSegment(sketch, "E373", {"start": v(-16.45, 0.9) * mm, "end": v(-14.64, 1.49) * mm});
            skLineSegment(sketch, "E374", {"start": v(-14.64, 1.49) * mm, "end": v(-12.6, 2.12) * mm});
            skLineSegment(sketch, "E375", {"start": v(-12.6, 2.12) * mm, "end": v(-11.1, 2.55) * mm});
            skLineSegment(sketch, "E376", {"start": v(-11.1, 2.55) * mm, "end": v(-9.55, 3.82) * mm});
            skLineSegment(sketch, "E377", {"start": v(-9.55, 3.82) * mm, "end": v(-8.04, 5.22) * mm});
            skLineSegment(sketch, "E378", {"start": v(-8.04, 5.22) * mm, "end": v(-6.68, 6.77) * mm});
            skLineSegment(sketch, "E379", {"start": v(-6.68, 6.77) * mm, "end": v(-5.8, 8.1) * mm});
            skLineSegment(sketch, "E380", {"start": v(-5.8, 8.1) * mm, "end": v(-5.33, 9.25) * mm});
            skLineSegment(sketch, "E381", {"start": v(-5.33, 9.25) * mm, "end": v(-4.8, 10.52) * mm});
            skLineSegment(sketch, "E382", {"start": v(-4.8, 10.52) * mm, "end": v(-4.29, 11.36) * mm});
            skLineSegment(sketch, "E383", {"start": v(-4.29, 11.36) * mm, "end": v(-4.07, 12.3) * mm});
            skLineSegment(sketch, "E384", {"start": v(-4.07, 12.3) * mm, "end": v(-5.89, 10.9) * mm});
            skLineSegment(sketch, "E385", {"start": v(-5.89, 10.9) * mm, "end": v(-7.46, 9.91) * mm});
            skLineSegment(sketch, "E386", {"start": v(-7.46, 9.91) * mm, "end": v(-8.08, 8.8) * mm});
            skLineSegment(sketch, "E387", {"start": v(-8.08, 8.8) * mm, "end": v(-8.96, 7.49) * mm});
            skLineSegment(sketch, "E388", {"start": v(-8.96, 7.49) * mm, "end": v(-10.36, 5.96) * mm});
            skLineSegment(sketch, "E389", {"start": v(-10.36, 5.96) * mm, "end": v(-11.94, 4.77) * mm});
            skLineSegment(sketch, "E390", {"start": v(-11.94, 4.77) * mm, "end": v(-13.13, 3.98) * mm});
            skLineSegment(sketch, "E391", {"start": v(-13.13, 3.98) * mm, "end": v(-14.55, 3.49) * mm});
            skLineSegment(sketch, "E392", {"start": v(-14.55, 3.49) * mm, "end": v(-16.1, 3.18) * mm});
            skLineSegment(sketch, "E393", {"start": v(-16.1, 3.18) * mm, "end": v(-17.85, 3) * mm});
            skLineSegment(sketch, "E394", {"start": v(-17.85, 3) * mm, "end": v(-19.77, 3.44) * mm});
            skLineSegment(sketch, "E395", {"start": v(-19.77, 3.44) * mm, "end": v(-21, 4.07) * mm});
            skLineSegment(sketch, "E396", {"start": v(-21, 4.07) * mm, "end": v(-22, 5.1) * mm});
            skLineSegment(sketch, "E397", {"start": v(-22, 5.1) * mm, "end": v(-22.6, 6.18) * mm});
            skLineSegment(sketch, "E398", {"start": v(-22.6, 6.18) * mm, "end": v(-23.07, 7.3) * mm});
            skLineSegment(sketch, "E399", {"start": v(-23.07, 7.3) * mm, "end": v(-23.26, 9.07) * mm});
            skLineSegment(sketch, "E400", {"start": v(-23.26, 9.07) * mm, "end": v(-22.97, 10.27) * mm});
            skLineSegment(sketch, "E401", {"start": v(-22.97, 10.27) * mm, "end": v(-22.04, 11.44) * mm});
            skLineSegment(sketch, "E402", {"start": v(-22.04, 11.44) * mm, "end": v(-20.58, 11.91) * mm});
            skLineSegment(sketch, "E403", {"start": v(-20.58, 11.91) * mm, "end": v(-19.19, 11.97) * mm});
            skLineSegment(sketch, "E404", {"start": v(-19.19, 11.97) * mm, "end": v(-18.16, 11.17) * mm});
            skLineSegment(sketch, "E405", {"start": v(-18.16, 11.17) * mm, "end": v(-18.14, 10.52) * mm});
            skLineSegment(sketch, "E406", {"start": v(-18.14, 10.52) * mm, "end": v(-18.71, 9.66) * mm});
            skLineSegment(sketch, "E407", {"start": v(-18.71, 9.66) * mm, "end": v(-19.47, 8.87) * mm});
            skLineSegment(sketch, "E408", {"start": v(-19.47, 8.87) * mm, "end": v(-20.18, 7.92) * mm});
            skLineSegment(sketch, "E409", {"start": v(-20.18, 7.92) * mm, "end": v(-20.45, 6.66) * mm});
            skLineSegment(sketch, "E410", {"start": v(-20.45, 6.66) * mm, "end": v(-20.15, 5.48) * mm});
            skLineSegment(sketch, "E411", {"start": v(-20.15, 5.48) * mm, "end": v(-18.9, 4.8) * mm});
            skLineSegment(sketch, "E412", {"start": v(-18.9, 4.8) * mm, "end": v(-17.55, 4.7) * mm});
            skLineSegment(sketch, "E413", {"start": v(-17.55, 4.7) * mm, "end": v(-16.38, 5.12) * mm});
            skLineSegment(sketch, "E414", {"start": v(-16.38, 5.12) * mm, "end": v(-14.95, 5.89) * mm});
            skLineSegment(sketch, "E415", {"start": v(-14.95, 5.89) * mm, "end": v(-13.57, 7.98) * mm});
            skLineSegment(sketch, "E416", {"start": v(-13.57, 7.98) * mm, "end": v(-13.39, 9.2) * mm});
            skLineSegment(sketch, "E417", {"start": v(-13.39, 9.2) * mm, "end": v(-13.7, 10.84) * mm});
            skLineSegment(sketch, "E418", {"start": v(-13.7, 10.84) * mm, "end": v(-14.25, 11.7) * mm});
            skLineSegment(sketch, "E419", {"start": v(-14.25, 11.7) * mm, "end": v(-14.76, 12.63) * mm});
            skLineSegment(sketch, "E420", {"start": v(-14.76, 12.63) * mm, "end": v(-16.16, 14.47) * mm});
            skLineSegment(sketch, "E421", {"start": v(-16.16, 14.47) * mm, "end": v(-16.6, 15.7) * mm});
            skLineSegment(sketch, "E422", {"start": v(-16.6, 15.7) * mm, "end": v(-16.75, 17.11) * mm});
            skLineSegment(sketch, "E423", {"start": v(-16.75, 17.11) * mm, "end": v(-16.78, 17.8) * mm});
            skLineSegment(sketch, "E424", {"start": v(-16.78, 17.8) * mm, "end": v(-16.66, 18.66) * mm});
            skLineSegment(sketch, "E425", {"start": v(-16.66, 18.66) * mm, "end": v(-16.33, 19.62) * mm});
            skLineSegment(sketch, "E426", {"start": v(-16.33, 19.62) * mm, "end": v(-16.04, 20.29) * mm});
            skLineSegment(sketch, "E427", {"start": v(-16.04, 20.29) * mm, "end": v(-15.71, 20.65) * mm});
            skLineSegment(sketch, "E428", {"start": v(-15.71, 20.65) * mm, "end": v(-15.37, 21.1) * mm});
            skLineSegment(sketch, "E429", {"start": v(-15.37, 21.1) * mm, "end": v(-14.73, 21.63) * mm});
            skLineSegment(sketch, "E430", {"start": v(-14.73, 21.63) * mm, "end": v(-14.22, 21.94) * mm});
            skLineSegment(sketch, "E431", {"start": v(-14.22, 21.94) * mm, "end": v(-13.72, 22.18) * mm});
            skLineSegment(sketch, "E432", {"start": v(-13.72, 22.18) * mm, "end": v(-12.1, 22.5) * mm});
            skLineSegment(sketch, "E433", {"start": v(-12.1, 22.5) * mm, "end": v(-11.3, 22.41) * mm});
            skLineSegment(sketch, "E434", {"start": v(-11.3, 22.41) * mm, "end": v(-10.7, 22.16) * mm});
            skLineSegment(sketch, "E435", {"start": v(-10.7, 22.16) * mm, "end": v(-10.3, 21.9) * mm});
            skLineSegment(sketch, "E436", {"start": v(-10.3, 21.9) * mm, "end": v(-9.96, 21.6) * mm});
            skLineSegment(sketch, "E437", {"start": v(-9.96, 21.6) * mm, "end": v(-9.67, 21.03) * mm});
            skLineSegment(sketch, "E438", {"start": v(-9.67, 21.03) * mm, "end": v(-9.42, 20.4) * mm});
            skLineSegment(sketch, "E439", {"start": v(-9.42, 20.4) * mm, "end": v(-9.5, 19.7) * mm});
            skLineSegment(sketch, "E440", {"start": v(-9.5, 19.7) * mm, "end": v(-9.7, 19.12) * mm});
            skLineSegment(sketch, "E441", {"start": v(-9.7, 19.12) * mm, "end": v(-9.94, 18.72) * mm});
            skLineSegment(sketch, "E442", {"start": v(-9.94, 18.72) * mm, "end": v(-10.28, 18.5) * mm});
            skLineSegment(sketch, "E443", {"start": v(-10.28, 18.5) * mm, "end": v(-11.32, 18.68) * mm});
            skLineSegment(sketch, "E444", {"start": v(-11.32, 18.68) * mm, "end": v(-12.25, 18.85) * mm});
            skLineSegment(sketch, "E445", {"start": v(-12.25, 18.85) * mm, "end": v(-12.76, 19.02) * mm});
            skLineSegment(sketch, "E446", {"start": v(-12.76, 19.02) * mm, "end": v(-13.34, 19.01) * mm});
            skLineSegment(sketch, "E447", {"start": v(-13.34, 19.01) * mm, "end": v(-14.02, 18.93) * mm});
            skLineSegment(sketch, "E448", {"start": v(-14.02, 18.93) * mm, "end": v(-14.55, 18.52) * mm});
            skLineSegment(sketch, "E449", {"start": v(-14.55, 18.52) * mm, "end": v(-15.28, 17.6) * mm});
            skLineSegment(sketch, "E450", {"start": v(-15.28, 17.6) * mm, "end": v(-15.5, 17.2) * mm});
            skLineSegment(sketch, "E451", {"start": v(-15.5, 17.2) * mm, "end": v(-15.62, 16.72) * mm});
            skLineSegment(sketch, "E452", {"start": v(-15.62, 16.72) * mm, "end": v(-15.61, 16) * mm});
            skLineSegment(sketch, "E453", {"start": v(-15.61, 16) * mm, "end": v(-15.54, 15.31) * mm});
            skLineSegment(sketch, "E454", {"start": v(-15.54, 15.31) * mm, "end": v(-15.17, 14.68) * mm});
            skLineSegment(sketch, "E455", {"start": v(-15.17, 14.68) * mm, "end": v(-14.62, 13.97) * mm});
            skLineSegment(sketch, "E456", {"start": v(-14.62, 13.97) * mm, "end": v(-12.86, 13.04) * mm});
            skLineSegment(sketch, "E457", {"start": v(-12.86, 13.04) * mm, "end": v(-11.55, 12.85) * mm});
            skLineSegment(sketch, "E458", {"start": v(-11.55, 12.85) * mm, "end": v(-10.54, 12.89) * mm});
            skLineSegment(sketch, "E459", {"start": v(-10.54, 12.89) * mm, "end": v(-9.52, 12.94) * mm});
            skLineSegment(sketch, "E460", {"start": v(-9.52, 12.94) * mm, "end": v(-8.8, 13.3) * mm});
            skLineSegment(sketch, "E461", {"start": v(-8.8, 13.3) * mm, "end": v(-7.77, 13.87) * mm});
            skLineSegment(sketch, "E462", {"start": v(-7.77, 13.87) * mm, "end": v(-7.22, 14.27) * mm});
            skLineSegment(sketch, "E463", {"start": v(-7.22, 14.27) * mm, "end": v(-6.54, 14.83) * mm});
            skLineSegment(sketch, "E464", {"start": v(-6.54, 14.83) * mm, "end": v(-5.88, 15.43) * mm});
            skLineSegment(sketch, "E465", {"start": v(-5.88, 15.43) * mm, "end": v(-5.5, 16.1) * mm});
            skLineSegment(sketch, "E466", {"start": v(-5.5, 16.1) * mm, "end": v(-5.16, 16.91) * mm});
            skLineSegment(sketch, "E467", {"start": v(-5.16, 16.91) * mm, "end": v(-4.79, 19.73) * mm});
            skLineSegment(sketch, "E468", {"start": v(-4.79, 19.73) * mm, "end": v(-4.83, 20.2) * mm});
            skLineSegment(sketch, "E469", {"start": v(-4.83, 20.2) * mm, "end": v(-4.93, 21.06) * mm});
            skLineSegment(sketch, "E470", {"start": v(-4.93, 21.06) * mm, "end": v(-5.12, 21.73) * mm});
            skLineSegment(sketch, "E471", {"start": v(-5.12, 21.73) * mm, "end": v(-5.84, 23.24) * mm});
            skLineSegment(sketch, "E472", {"start": v(-5.84, 23.24) * mm, "end": v(-6.36, 24.46) * mm});
            skLineSegment(sketch, "E473", {"start": v(-6.36, 24.46) * mm, "end": v(-7.08, 25.5) * mm});
            skLineSegment(sketch, "E474", {"start": v(-7.08, 25.5) * mm, "end": v(-8.03, 26.65) * mm});
            skLineSegment(sketch, "E475", {"start": v(-8.03, 26.65) * mm, "end": v(-8.85, 27.4) * mm});
            skLineSegment(sketch, "E476", {"start": v(-8.85, 27.4) * mm, "end": v(-9.96, 28.04) * mm});
            skLineSegment(sketch, "E477", {"start": v(-9.96, 28.04) * mm, "end": v(-10.96, 28.66) * mm});
            skLineSegment(sketch, "E478", {"start": v(-10.96, 28.66) * mm, "end": v(-12.47, 29.38) * mm});
            skLineSegment(sketch, "E479", {"start": v(-12.47, 29.38) * mm, "end": v(-13.7, 29.86) * mm});
            skLineSegment(sketch, "E480", {"start": v(-13.7, 29.86) * mm, "end": v(-15.2, 30.2) * mm});
            skLineSegment(sketch, "E481", {"start": v(-15.2, 30.2) * mm, "end": v(-16.44, 30.4) * mm});
            skLineSegment(sketch, "E482", {"start": v(-16.44, 30.4) * mm, "end": v(-16.93, 30.48) * mm});
            skLineSegment(sketch, "E483", {"start": v(-16.93, 30.48) * mm, "end": v(-18.08, 30.5) * mm});
            skLineSegment(sketch, "E484", {"start": v(-18.08, 30.5) * mm, "end": v(-18.82, 30.5) * mm});
            skLineSegment(sketch, "E485", {"start": v(-18.82, 30.5) * mm, "end": v(-19.85, 30.44) * mm});
            skLineSegment(sketch, "E486", {"start": v(-19.85, 30.44) * mm, "end": v(-21.02, 30.32) * mm});
            skLineSegment(sketch, "E487", {"start": v(-21.02, 30.32) * mm, "end": v(-21.76, 30.24) * mm});
            skLineSegment(sketch, "E488", {"start": v(-21.76, 30.24) * mm, "end": v(-22.64, 30.07) * mm});
            skLineSegment(sketch, "E489", {"start": v(-22.64, 30.07) * mm, "end": v(-22.26, 30.05) * mm});
            skLineSegment(sketch, "E490", {"start": v(-22.26, 30.05) * mm, "end": v(-21.44, 30.04) * mm});
            skLineSegment(sketch, "E491", {"start": v(-21.44, 30.04) * mm, "end": v(-20.8, 29.94) * mm});
            skLineSegment(sketch, "E492", {"start": v(-20.8, 29.94) * mm, "end": v(-20, 29.72) * mm});
            skLineSegment(sketch, "E493", {"start": v(-20, 29.72) * mm, "end": v(-19.33, 29.44) * mm});
            skLineSegment(sketch, "E494", {"start": v(-19.33, 29.44) * mm, "end": v(-18.85, 29.24) * mm});
            skLineSegment(sketch, "E495", {"start": v(-18.85, 29.24) * mm, "end": v(-18.39, 28.99) * mm});
            skLineSegment(sketch, "E496", {"start": v(-18.39, 28.99) * mm, "end": v(-18, 28.6) * mm});
            skLineSegment(sketch, "E497", {"start": v(-18, 28.6) * mm, "end": v(-17.7, 28.3) * mm});
            skLineSegment(sketch, "E498", {"start": v(-17.7, 28.3) * mm, "end": v(-17.59, 28.18) * mm});
            skLineSegment(sketch, "E499", {"start": v(-21.55, 17.02) * mm, "end": v(-22.38, 17.25) * mm});
            skLineSegment(sketch, "E500", {"start": v(-22.38, 17.25) * mm, "end": v(-22.93, 17.59) * mm});
            skLineSegment(sketch, "E501", {"start": v(-22.93, 17.59) * mm, "end": v(-23.33, 18) * mm});
            skSolve(sketch);
        }
        {
            var Q0;
            Q0=qCreatedBy(makeId("Front.planeOp"),FACE);
            var sketch = newSketch(context, id + "F2", { "sketchPlane" : qUnion([Q0])});
            skLineSegment(sketch, "E502", {"start": v(-10.58, 10.8) * mm, "end": v(-10.25, 10.44) * mm});
            skLineSegment(sketch, "E503", {"start": v(-10.25, 10.44) * mm, "end": v(-9.81, 10.13) * mm});
            skLineSegment(sketch, "E504", {"start": v(-9.81, 10.13) * mm, "end": v(-9.18, 9.95) * mm});
            skLineSegment(sketch, "E505", {"start": v(-9.18, 9.95) * mm, "end": v(-8.59, 9.88) * mm});
            skLineSegment(sketch, "E506", {"start": v(-8.59, 9.88) * mm, "end": v(-7.96, 9.85) * mm});
            skLineSegment(sketch, "E507", {"start": v(-7.96, 9.85) * mm, "end": v(-7.48, 10) * mm});
            skLineSegment(sketch, "E508", {"start": v(-7.48, 10) * mm, "end": v(-6.35, 10.55) * mm});
            skLineSegment(sketch, "E509", {"start": v(-6.35, 10.55) * mm, "end": v(-5.2, 11.23) * mm});
            skLineSegment(sketch, "E510", {"start": v(-5.2, 11.23) * mm, "end": v(-4.46, 11.85) * mm});
            skLineSegment(sketch, "E511", {"start": v(-4.46, 11.85) * mm, "end": v(-3.71, 12.8) * mm});
            skLineSegment(sketch, "E512", {"start": v(-3.71, 12.8) * mm, "end": v(-2.9, 14.59) * mm});
            skLineSegment(sketch, "E513", {"start": v(-2.9, 14.59) * mm, "end": v(-2.83, 15.16) * mm});
            skLineSegment(sketch, "E514", {"start": v(-2.83, 15.16) * mm, "end": v(-2.83, 16.62) * mm});
            skLineSegment(sketch, "E515", {"start": v(-2.83, 16.62) * mm, "end": v(-2.9, 17.5) * mm});
            skLineSegment(sketch, "E516", {"start": v(-2.9, 17.5) * mm, "end": v(-2.9, 17.52) * mm});
            skLineSegment(sketch, "E517", {"start": v(-3.45, 20.18) * mm, "end": v(-3.66, 20.88) * mm});
            skLineSegment(sketch, "E518", {"start": v(-3.66, 20.88) * mm, "end": v(-4.29, 21.96) * mm});
            skLineSegment(sketch, "E519", {"start": v(-4.29, 21.96) * mm, "end": v(-5, 22.88) * mm});
            skLineSegment(sketch, "E520", {"start": v(-5, 22.88) * mm, "end": v(-5.53, 23.65) * mm});
            skLineSegment(sketch, "E521", {"start": v(-5.53, 23.65) * mm, "end": v(-6.14, 24.55) * mm});
            skLineSegment(sketch, "E522", {"start": v(-6.14, 24.55) * mm, "end": v(-6.62, 25.28) * mm});
            skLineSegment(sketch, "E523", {"start": v(-6.62, 25.28) * mm, "end": v(-7.14, 25.82) * mm});
            skLineSegment(sketch, "E524", {"start": v(-6.52, 24.5) * mm, "end": v(-6.19, 23.78) * mm});
            skLineSegment(sketch, "E525", {"start": v(-6.19, 23.78) * mm, "end": v(-5.7, 22.8) * mm});
            skLineSegment(sketch, "E526", {"start": v(-5.7, 22.8) * mm, "end": v(-5.2, 21.9) * mm});
            skLineSegment(sketch, "E527", {"start": v(-5.2, 21.9) * mm, "end": v(-4.9, 21.14) * mm});
            skLineSegment(sketch, "E528", {"start": v(-4.9, 21.14) * mm, "end": v(-4.66, 20.62) * mm});
            skLineSegment(sketch, "E529", {"start": v(-4.66, 20.62) * mm, "end": v(-4.45, 19.5) * mm});
            skLineSegment(sketch, "E530", {"start": v(-4.28, 16.81) * mm, "end": v(-4.57, 15.5) * mm});
            skLineSegment(sketch, "E531", {"start": v(-4.57, 15.5) * mm, "end": v(-5.03, 14.58) * mm});
            skLineSegment(sketch, "E532", {"start": v(-5.03, 14.58) * mm, "end": v(-5.6, 13.88) * mm});
            skLineSegment(sketch, "E533", {"start": v(-5.6, 13.88) * mm, "end": v(-6.98, 12.54) * mm});
            skLineSegment(sketch, "E534", {"start": v(-6.98, 12.54) * mm, "end": v(-7.57, 12.08) * mm});
            skLineSegment(sketch, "E535", {"start": v(-7.57, 12.08) * mm, "end": v(-8.34, 11.5) * mm});
            skLineSegment(sketch, "E536", {"start": v(-8.34, 11.5) * mm, "end": v(-9.26, 11.12) * mm});
            skLineSegment(sketch, "E537", {"start": v(-9.26, 11.12) * mm, "end": v(-9.98, 10.87) * mm});
            skLineSegment(sketch, "E538", {"start": v(-9.98, 10.87) * mm, "end": v(-10.58, 10.8) * mm});
            skLineSegment(sketch, "E539", {"start": v(-4.28, 16.81) * mm, "end": v(-4.45, 19.5) * mm});
            skLineSegment(sketch, "E540", {"start": v(-2.9, 17.52) * mm, "end": v(-3.11, 18.98) * mm});
            skLineSegment(sketch, "E541", {"start": v(-3.11, 18.98) * mm, "end": v(-3.45, 20.18) * mm});
            skLineSegment(sketch, "E542", {"start": v(-30.37, 6.16) * mm, "end": v(-30.04, 5.66) * mm});
            skLineSegment(sketch, "E543", {"start": v(-30.04, 5.66) * mm, "end": v(-29.46, 4.94) * mm});
            skLineSegment(sketch, "E544", {"start": v(-29.46, 4.94) * mm, "end": v(-28.77, 4.3) * mm});
            skLineSegment(sketch, "E545", {"start": v(-28.77, 4.3) * mm, "end": v(-27.98, 3.66) * mm});
            skLineSegment(sketch, "E546", {"start": v(-27.98, 3.66) * mm, "end": v(-27.08, 3.06) * mm});
            skLineSegment(sketch, "E547", {"start": v(-27.08, 3.06) * mm, "end": v(-26.12, 2.45) * mm});
            skLineSegment(sketch, "E548", {"start": v(-26.12, 2.45) * mm, "end": v(-24.77, 1.75) * mm});
            skLineSegment(sketch, "E549", {"start": v(-24.77, 1.75) * mm, "end": v(-23.6, 1.32) * mm});
            skLineSegment(sketch, "E550", {"start": v(-23.6, 1.32) * mm, "end": v(-22.42, 1.04) * mm});
            skLineSegment(sketch, "E551", {"start": v(-22.42, 1.04) * mm, "end": v(-21.44, 0.8) * mm});
            skLineSegment(sketch, "E552", {"start": v(-21.44, 0.8) * mm, "end": v(-20, 0.8) * mm});
            skLineSegment(sketch, "E553", {"start": v(-20, 0.8) * mm, "end": v(-18.8, 0.8) * mm});
            skLineSegment(sketch, "E554", {"start": v(-18.8, 0.8) * mm, "end": v(-18.39, 0.8) * mm});
            skLineSegment(sketch, "E555", {"start": v(-18.39, 0.8) * mm, "end": v(-20.67, 1.02) * mm});
            skLineSegment(sketch, "E556", {"start": v(-20.67, 1.02) * mm, "end": v(-22.13, 1.36) * mm});
            skLineSegment(sketch, "E557", {"start": v(-22.13, 1.36) * mm, "end": v(-23.25, 1.67) * mm});
            skLineSegment(sketch, "E558", {"start": v(-23.25, 1.67) * mm, "end": v(-24.43, 2.29) * mm});
            skLineSegment(sketch, "E559", {"start": v(-24.43, 2.29) * mm, "end": v(-25.14, 2.84) * mm});
            skLineSegment(sketch, "E560", {"start": v(-25.14, 2.84) * mm, "end": v(-26.17, 3.65) * mm});
            skLineSegment(sketch, "E561", {"start": v(-26.17, 3.65) * mm, "end": v(-26.96, 4.66) * mm});
            skLineSegment(sketch, "E562", {"start": v(-26.96, 4.66) * mm, "end": v(-27.54, 5.6) * mm});
            skLineSegment(sketch, "E563", {"start": v(-27.54, 5.6) * mm, "end": v(-27.86, 6.77) * mm});
            skLineSegment(sketch, "E564", {"start": v(-27.86, 6.77) * mm, "end": v(-28.02, 7.57) * mm});
            skLineSegment(sketch, "E565", {"start": v(-28.02, 7.57) * mm, "end": v(-28.02, 8.61) * mm});
            skLineSegment(sketch, "E566", {"start": v(-28.02, 8.61) * mm, "end": v(-27.96, 9.39) * mm});
            skLineSegment(sketch, "E567", {"start": v(-27.96, 9.39) * mm, "end": v(-27.8, 10.2) * mm});
            skLineSegment(sketch, "E568", {"start": v(-27.8, 10.2) * mm, "end": v(-27.68, 10.74) * mm});
            skLineSegment(sketch, "E569", {"start": v(-27.68, 10.74) * mm, "end": v(-27.38, 11.45) * mm});
            skLineSegment(sketch, "E570", {"start": v(-27.38, 11.45) * mm, "end": v(-27.17, 11.86) * mm});
            skLineSegment(sketch, "E571", {"start": v(-27.17, 11.86) * mm, "end": v(-27.8, 11.69) * mm});
            skLineSegment(sketch, "E572", {"start": v(-27.8, 11.69) * mm, "end": v(-28.33, 11.45) * mm});
            skLineSegment(sketch, "E573", {"start": v(-28.33, 11.45) * mm, "end": v(-29.06, 11.1) * mm});
            skLineSegment(sketch, "E574", {"start": v(-29.06, 11.1) * mm, "end": v(-29.68, 10.51) * mm});
            skLineSegment(sketch, "E575", {"start": v(-29.68, 10.51) * mm, "end": v(-30.04, 10.1) * mm});
            skLineSegment(sketch, "E576", {"start": v(-30.04, 10.1) * mm, "end": v(-30.32, 9.76) * mm});
            skLineSegment(sketch, "E577", {"start": v(-30.32, 9.76) * mm, "end": v(-30.53, 9.26) * mm});
            skLineSegment(sketch, "E578", {"start": v(-30.53, 9.26) * mm, "end": v(-30.8, 8.64) * mm});
            skLineSegment(sketch, "E579", {"start": v(-30.8, 8.64) * mm, "end": v(-30.87, 7.98) * mm});
            skLineSegment(sketch, "E580", {"start": v(-30.87, 7.98) * mm, "end": v(-30.83, 7.33) * mm});
            skLineSegment(sketch, "E581", {"start": v(-30.83, 7.33) * mm, "end": v(-30.64, 6.85) * mm});
            skLineSegment(sketch, "E582", {"start": v(-30.64, 6.85) * mm, "end": v(-30.37, 6.16) * mm});
            skPoint(sketch, "E583.start.orphan", {"position": v(-7.66, 26.37) * mm});
            skLineSegment(sketch, "E584", {"start": v(-6.19, 23.78) * mm, "end": v(-6.52, 24.5) * mm});
            skLineSegment(sketch, "E585", {"start": v(-6.52, 24.5) * mm, "end": v(-6.85, 25.05) * mm});
            skLineSegment(sketch, "E586", {"start": v(-6.85, 25.05) * mm, "end": v(-7.18, 25.58) * mm});
            skLineSegment(sketch, "E587", {"start": v(-7.18, 25.58) * mm, "end": v(-7.55, 26.02) * mm});
            skLineSegment(sketch, "E588", {"start": v(-7.55, 26.02) * mm, "end": v(-7.93, 26.48) * mm});
            skLineSegment(sketch, "E589", {"start": v(-7.93, 26.48) * mm, "end": v(-8.1, 26.67) * mm});
            skLineSegment(sketch, "E590", {"start": v(-8.1, 26.67) * mm, "end": v(-7.14, 25.82) * mm});
            skSolve(sketch);
        }
        {
            var Q0;
            Q0 = qSketchRegion(id + "F2", true);
            var Q1;
            Q1 = qSketchRegion(id + "F0", true);
            var Q2;
            Q2 = qSketchRegion(id + "F1", true);
            extrude(context, id + "F3", {"entities" : qUnion([Q0, Q1, Q2]), "depth" : 5 * mm, "offsetDistance" : 25 * mm});
        }
        {
            var Q0;
            Q0=qCreatedBy(makeId("Front.planeOp"),FACE);
            var sketch = newSketch(context, id + "F4", { "sketchPlane" : qUnion([Q0])});
            skLineSegment(sketch, "E591", {"start": v(-18.31, 15.77) * mm, "end": v(-18.31, -3.73) * mm, "construction": true});
            skLineSegment(sketch, "E592", {"start": v(-18.31, 15.77) * mm, "end": v(8.19, 15.77) * mm, "construction": true});
            skSolve(sketch);
        }
        {
            var Q0;
            Q0=qCreatedBy(makeId("Top.planeOp"),FACE);
            cPlane(context, id + "F5", {"entities" : qUnion([Q0]), "cplaneType" : CPlaneType.OFFSET, "offset" : 15.7 * mm, "width" : 150 * mm, "height" : 150 * mm});
        }
        {
            var Q0;
            Q0=qCreatedBy(id+"F5.planeOp",FACE);
            var sketch = newSketch(context, id + "F6", { "sketchPlane" : qUnion([Q0])});
            skArc(sketch, "E593", {"start": v(-54.54, 31.52) * mm, "mid": v(-18.58, -4.43) * mm, "end": v(17.37, 31.52) * mm});
            skPoint(sketch, "E593.first.point", {"position": v(-35.88, 0) * mm});
            skPoint(sketch, "E593.second.point", {"position": v(-1.29, 0) * mm});
            skPoint(sketch, "E593.third.point", {"position": v(-17.07, -4.4) * mm});
            skLineSegment(sketch, "E594", {"start": v(-18.58, 31.52) * mm, "end": v(17.37, 31.52) * mm});
            skLineSegment(sketch, "E595", {"start": v(17.37, 31.52) * mm, "end": v(-54.54, 31.52) * mm});
            skSolve(sketch);
        }
        {
            var Q0;
            Q0 = qSketchRegion(id + "F6", true);
            var Q1;
            Q1=sQuery(id+"F6.wireOp",EDGE,"E595");
            revolve(context, id + "F7", {"entities" : qUnion([Q0]), "axis" : qUnion([Q1]), "revolveType" : RevolveType.FULL});
        }
        {
            var Q0;
            Q0=makeQuery(id+"F7.opRevolve","SWEPT_BODY",BODY,{"disambiguationData":[OSD([sQuery(id+"F6.wireOp",EDGE,"E593"),sQuery(id+"F6.wireOp",EDGE,"E595")])]});
            var Q1;
            Q1=makeQuery(id+"F3.opExtrude","SWEPT_BODY",BODY,{"disambiguationData":[OSD([sQuery(id+"F0.wireOp",EDGE,"E0"),sQuery(id+"F0.wireOp",EDGE,"E1"),sQuery(id+"F0.wireOp",EDGE,"E2"),sQuery(id+"F0.wireOp",EDGE,"E3"),sQuery(id+"F0.wireOp",EDGE,"E4"),sQuery(id+"F0.wireOp",EDGE,"E5"),sQuery(id+"F0.wireOp",EDGE,"E6"),sQuery(id+"F0.wireOp",EDGE,"E7"),sQuery(id+"F0.wireOp",EDGE,"E8"),sQuery(id+"F0.wireOp",EDGE,"E94"),sQuery(id+"F0.wireOp",EDGE,"E95"),sQuery(id+"F0.wireOp",EDGE,"E96"),sQuery(id+"F0.wireOp",EDGE,"E97"),sQuery(id+"F0.wireOp",EDGE,"E98"),sQuery(id+"F0.wireOp",EDGE,"E99"),sQuery(id+"F0.wireOp",EDGE,"E100"),sQuery(id+"F0.wireOp",EDGE,"E101"),sQuery(id+"F0.wireOp",EDGE,"E102"),sQuery(id+"F0.wireOp",EDGE,"E103"),sQuery(id+"F0.wireOp",EDGE,"E104"),sQuery(id+"F0.wireOp",EDGE,"E105"),sQuery(id+"F0.wireOp",EDGE,"E106"),sQuery(id+"F0.wireOp",EDGE,"E107"),sQuery(id+"F0.wireOp",EDGE,"E108"),sQuery(id+"F0.wireOp",EDGE,"E109"),sQuery(id+"F0.wireOp",EDGE,"E110"),sQuery(id+"F0.wireOp",EDGE,"E111"),sQuery(id+"F0.wireOp",EDGE,"E112"),sQuery(id+"F0.wireOp",EDGE,"E113"),sQuery(id+"F0.wireOp",EDGE,"E114"),sQuery(id+"F0.wireOp",EDGE,"E115"),sQuery(id+"F0.wireOp",EDGE,"E116"),sQuery(id+"F0.wireOp",EDGE,"E117"),sQuery(id+"F0.wireOp",EDGE,"E118"),sQuery(id+"F0.wireOp",EDGE,"E119"),sQuery(id+"F0.wireOp",EDGE,"E120")])]});
            booleanBodies(context, id + "F8", {"operationType" : BooleanOperationType.INTERSECTION, "tools" : qUnion([Q0, Q1])});
        }
        {
            var Q0;
            Q0=makeQuery(id+"F8.opBoolean","INTERSECT",BODY,{"derivedFrom":[makeQuery(id+"F3.opExtrude","SWEPT_BODY",BODY,{"disambiguationData":[OSD([sQuery(id+"F0.wireOp",EDGE,"E0"),sQuery(id+"F0.wireOp",EDGE,"E1"),sQuery(id+"F0.wireOp",EDGE,"E2"),sQuery(id+"F0.wireOp",EDGE,"E3"),sQuery(id+"F0.wireOp",EDGE,"E4"),sQuery(id+"F0.wireOp",EDGE,"E5"),sQuery(id+"F0.wireOp",EDGE,"E6"),sQuery(id+"F0.wireOp",EDGE,"E7"),sQuery(id+"F0.wireOp",EDGE,"E8"),sQuery(id+"F0.wireOp",EDGE,"E94"),sQuery(id+"F0.wireOp",EDGE,"E95"),sQuery(id+"F0.wireOp",EDGE,"E96"),sQuery(id+"F0.wireOp",EDGE,"E97"),sQuery(id+"F0.wireOp",EDGE,"E98"),sQuery(id+"F0.wireOp",EDGE,"E99"),sQuery(id+"F0.wireOp",EDGE,"E100"),sQuery(id+"F0.wireOp",EDGE,"E101"),sQuery(id+"F0.wireOp",EDGE,"E102"),sQuery(id+"F0.wireOp",EDGE,"E103"),sQuery(id+"F0.wireOp",EDGE,"E104"),sQuery(id+"F0.wireOp",EDGE,"E105"),sQuery(id+"F0.wireOp",EDGE,"E106"),sQuery(id+"F0.wireOp",EDGE,"E107"),sQuery(id+"F0.wireOp",EDGE,"E108"),sQuery(id+"F0.wireOp",EDGE,"E109"),sQuery(id+"F0.wireOp",EDGE,"E110"),sQuery(id+"F0.wireOp",EDGE,"E111"),sQuery(id+"F0.wireOp",EDGE,"E112"),sQuery(id+"F0.wireOp",EDGE,"E113"),sQuery(id+"F0.wireOp",EDGE,"E114"),sQuery(id+"F0.wireOp",EDGE,"E115"),sQuery(id+"F0.wireOp",EDGE,"E116"),sQuery(id+"F0.wireOp",EDGE,"E117"),sQuery(id+"F0.wireOp",EDGE,"E118"),sQuery(id+"F0.wireOp",EDGE,"E119"),sQuery(id+"F0.wireOp",EDGE,"E120")])]}),makeQuery(id+"F7.opRevolve","SWEPT_BODY",BODY,{"disambiguationData":[OSD([sQuery(id+"F6.wireOp",EDGE,"E593"),sQuery(id+"F6.wireOp",EDGE,"E595")])]})]});
            var Q1;
            Q1=sQuery(id+"F4.wireOp",VERTEX,"E592.start");
            transform(context, id + "F9", {"entities" : qUnion([Q0]), "transformType" : TransformType.SCALE_UNIFORMLY, "scale" : .8, "scalePoint" : qUnion([Q1]), "makeCopy" : false});
        }
        {
            var Q0;
            Q0=qCreatedBy(makeId("Front.planeOp"),FACE);
            var sketch = newSketch(context, id + "F10", { "sketchPlane" : qUnion([Q0])});
            skText(sketch, "E596", { "text": "Hockey\nLegend", "fontName": "RobotoSlab-Bold.ttf"});
            const initialGuessF10  = {"E596": [-0.00481, 0.00958, 1, 0, 0.00693]};
            skSetInitialGuess(sketch, initialGuessF10);
            skSolve(sketch);
        }
        {
            var Q0;
            Q0 = qSketchRegion(id + "F10", true);
            extrude(context, id + "F11", {"entities" : qUnion([Q0]), "depth" : 3 * mm, "offsetDistance" : 25 * mm});
        }
        {
            var Q0;
            Q0=makeQuery(id+"F11.opExtrude","SWEPT_BODY",BODY,{"disambiguationData":[OSD([sQuery(id+"F10.wireOp",EDGE,"E596.sketch_text.stroke-0"),sQuery(id+"F10.wireOp",EDGE,"E596.sketch_text.stroke-1"),sQuery(id+"F10.wireOp",EDGE,"E596.sketch_text.stroke-2"),sQuery(id+"F10.wireOp",EDGE,"E596.sketch_text.stroke-3"),sQuery(id+"F10.wireOp",EDGE,"E596.sketch_text.stroke-4"),sQuery(id+"F10.wireOp",EDGE,"E596.sketch_text.stroke-5"),sQuery(id+"F10.wireOp",EDGE,"E596.sketch_text.stroke-6"),sQuery(id+"F10.wireOp",EDGE,"E596.sketch_text.stroke-7"),sQuery(id+"F10.wireOp",EDGE,"E596.sketch_text.stroke-8"),sQuery(id+"F10.wireOp",EDGE,"E596.sketch_text.stroke-9"),sQuery(id+"F10.wireOp",EDGE,"E596.sketch_text.stroke-10"),sQuery(id+"F10.wireOp",EDGE,"E596.sketch_text.stroke-11"),sQuery(id+"F10.wireOp",EDGE,"E596.sketch_text.stroke-12"),sQuery(id+"F10.wireOp",EDGE,"E596.sketch_text.stroke-13"),sQuery(id+"F10.wireOp",EDGE,"E596.sketch_text.stroke-14"),sQuery(id+"F10.wireOp",EDGE,"E596.sketch_text.stroke-15"),sQuery(id+"F10.wireOp",EDGE,"E596.sketch_text.stroke-16"),sQuery(id+"F10.wireOp",EDGE,"E596.sketch_text.stroke-17"),sQuery(id+"F10.wireOp",EDGE,"E596.sketch_text.stroke-18"),sQuery(id+"F10.wireOp",EDGE,"E596.sketch_text.stroke-19"),sQuery(id+"F10.wireOp",EDGE,"E596.sketch_text.stroke-20"),sQuery(id+"F10.wireOp",EDGE,"E596.sketch_text.stroke-21"),sQuery(id+"F10.wireOp",EDGE,"E596.sketch_text.stroke-22"),sQuery(id+"F10.wireOp",EDGE,"E596.sketch_text.stroke-23"),sQuery(id+"F10.wireOp",EDGE,"E596.sketch_text.stroke-24"),sQuery(id+"F10.wireOp",EDGE,"E596.sketch_text.stroke-25"),sQuery(id+"F10.wireOp",EDGE,"E596.sketch_text.stroke-26"),sQuery(id+"F10.wireOp",EDGE,"E596.sketch_text.stroke-27"),sQuery(id+"F10.wireOp",EDGE,"E596.sketch_text.stroke-28"),sQuery(id+"F10.wireOp",EDGE,"E596.sketch_text.stroke-29")])]});
            transform(context, id + "F12", {"entities" : qUnion([Q0]), "transformType" : TransformType.TRANSLATION_3D, "dx" : -2.18 * mm, "dy" : 0 * mm, "dz" : 1.42 * mm, "makeCopy" : false});
        }
        {
            var Q0;
            Q0=makeQuery(id+"F11.opExtrude","SWEPT_BODY",BODY,{"disambiguationData":[OSD([sQuery(id+"F10.wireOp",EDGE,"E596.sketch_text.stroke-30"),sQuery(id+"F10.wireOp",EDGE,"E596.sketch_text.stroke-31"),sQuery(id+"F10.wireOp",EDGE,"E596.sketch_text.stroke-32"),sQuery(id+"F10.wireOp",EDGE,"E596.sketch_text.stroke-33"),sQuery(id+"F10.wireOp",EDGE,"E596.sketch_text.stroke-34"),sQuery(id+"F10.wireOp",EDGE,"E596.sketch_text.stroke-35"),sQuery(id+"F10.wireOp",EDGE,"E596.sketch_text.stroke-36"),sQuery(id+"F10.wireOp",EDGE,"E596.sketch_text.stroke-37"),sQuery(id+"F10.wireOp",EDGE,"E596.sketch_text.stroke-38"),sQuery(id+"F10.wireOp",EDGE,"E596.sketch_text.stroke-39"),sQuery(id+"F10.wireOp",EDGE,"E596.sketch_text.stroke-40"),sQuery(id+"F10.wireOp",EDGE,"E596.sketch_text.stroke-41"),sQuery(id+"F10.wireOp",EDGE,"E596.sketch_text.stroke-42"),sQuery(id+"F10.wireOp",EDGE,"E596.sketch_text.stroke-43"),sQuery(id+"F10.wireOp",EDGE,"E596.sketch_text.stroke-44"),sQuery(id+"F10.wireOp",EDGE,"E596.sketch_text.stroke-45"),sQuery(id+"F10.wireOp",EDGE,"E596.sketch_text.stroke-46"),sQuery(id+"F10.wireOp",EDGE,"E596.sketch_text.stroke-47"),sQuery(id+"F10.wireOp",EDGE,"E596.sketch_text.stroke-48"),sQuery(id+"F10.wireOp",EDGE,"E596.sketch_text.stroke-49")])]});
            transform(context, id + "F13", {"entities" : qUnion([Q0]), "transformType" : TransformType.TRANSLATION_3D, "dx" : -3.55 * mm, "dy" : 0 * mm, "dz" : 1.6 * mm, "makeCopy" : false});
        }
        {
            var Q0;
            Q0=makeQuery(id+"F11.opExtrude","SWEPT_BODY",BODY,{"disambiguationData":[OSD([sQuery(id+"F10.wireOp",EDGE,"E596.sketch_text.stroke-50"),sQuery(id+"F10.wireOp",EDGE,"E596.sketch_text.stroke-51"),sQuery(id+"F10.wireOp",EDGE,"E596.sketch_text.stroke-52"),sQuery(id+"F10.wireOp",EDGE,"E596.sketch_text.stroke-53"),sQuery(id+"F10.wireOp",EDGE,"E596.sketch_text.stroke-54"),sQuery(id+"F10.wireOp",EDGE,"E596.sketch_text.stroke-55"),sQuery(id+"F10.wireOp",EDGE,"E596.sketch_text.stroke-56"),sQuery(id+"F10.wireOp",EDGE,"E596.sketch_text.stroke-57"),sQuery(id+"F10.wireOp",EDGE,"E596.sketch_text.stroke-58"),sQuery(id+"F10.wireOp",EDGE,"E596.sketch_text.stroke-59"),sQuery(id+"F10.wireOp",EDGE,"E596.sketch_text.stroke-60"),sQuery(id+"F10.wireOp",EDGE,"E596.sketch_text.stroke-61"),sQuery(id+"F10.wireOp",EDGE,"E596.sketch_text.stroke-62"),sQuery(id+"F10.wireOp",EDGE,"E596.sketch_text.stroke-63"),sQuery(id+"F10.wireOp",EDGE,"E596.sketch_text.stroke-64"),sQuery(id+"F10.wireOp",EDGE,"E596.sketch_text.stroke-65"),sQuery(id+"F10.wireOp",EDGE,"E596.sketch_text.stroke-66"),sQuery(id+"F10.wireOp",EDGE,"E596.sketch_text.stroke-67"),sQuery(id+"F10.wireOp",EDGE,"E596.sketch_text.stroke-68"),sQuery(id+"F10.wireOp",EDGE,"E596.sketch_text.stroke-69"),sQuery(id+"F10.wireOp",EDGE,"E596.sketch_text.stroke-70"),sQuery(id+"F10.wireOp",EDGE,"E596.sketch_text.stroke-71"),sQuery(id+"F10.wireOp",EDGE,"E596.sketch_text.stroke-72")])]});
            transform(context, id + "F14", {"entities" : qUnion([Q0]), "transformType" : TransformType.TRANSLATION_3D, "dx" : -4.78 * mm, "dy" : 0 * mm, "dz" : 1.6 * mm, "makeCopy" : false});
        }
        {
            var Q0;
            Q0=makeQuery(id+"F11.opExtrude","SWEPT_BODY",BODY,{"disambiguationData":[OSD([sQuery(id+"F10.wireOp",EDGE,"E596.sketch_text.stroke-73"),sQuery(id+"F10.wireOp",EDGE,"E596.sketch_text.stroke-74"),sQuery(id+"F10.wireOp",EDGE,"E596.sketch_text.stroke-75"),sQuery(id+"F10.wireOp",EDGE,"E596.sketch_text.stroke-76"),sQuery(id+"F10.wireOp",EDGE,"E596.sketch_text.stroke-77"),sQuery(id+"F10.wireOp",EDGE,"E596.sketch_text.stroke-78"),sQuery(id+"F10.wireOp",EDGE,"E596.sketch_text.stroke-79"),sQuery(id+"F10.wireOp",EDGE,"E596.sketch_text.stroke-80"),sQuery(id+"F10.wireOp",EDGE,"E596.sketch_text.stroke-81"),sQuery(id+"F10.wireOp",EDGE,"E596.sketch_text.stroke-82"),sQuery(id+"F10.wireOp",EDGE,"E596.sketch_text.stroke-83"),sQuery(id+"F10.wireOp",EDGE,"E596.sketch_text.stroke-84"),sQuery(id+"F10.wireOp",EDGE,"E596.sketch_text.stroke-85"),sQuery(id+"F10.wireOp",EDGE,"E596.sketch_text.stroke-86"),sQuery(id+"F10.wireOp",EDGE,"E596.sketch_text.stroke-87"),sQuery(id+"F10.wireOp",EDGE,"E596.sketch_text.stroke-88"),sQuery(id+"F10.wireOp",EDGE,"E596.sketch_text.stroke-89"),sQuery(id+"F10.wireOp",EDGE,"E596.sketch_text.stroke-90"),sQuery(id+"F10.wireOp",EDGE,"E596.sketch_text.stroke-91"),sQuery(id+"F10.wireOp",EDGE,"E596.sketch_text.stroke-92"),sQuery(id+"F10.wireOp",EDGE,"E596.sketch_text.stroke-93"),sQuery(id+"F10.wireOp",EDGE,"E596.sketch_text.stroke-94"),sQuery(id+"F10.wireOp",EDGE,"E596.sketch_text.stroke-95"),sQuery(id+"F10.wireOp",EDGE,"E596.sketch_text.stroke-96"),sQuery(id+"F10.wireOp",EDGE,"E596.sketch_text.stroke-97"),sQuery(id+"F10.wireOp",EDGE,"E596.sketch_text.stroke-98"),sQuery(id+"F10.wireOp",EDGE,"E596.sketch_text.stroke-99")])]});
            transform(context, id + "F15", {"entities" : qUnion([Q0]), "transformType" : TransformType.TRANSLATION_3D, "dx" : -6.1 * mm, "dy" : 0 * mm, "dz" : 1.6 * mm, "makeCopy" : false});
        }
        {
            var Q0;
            Q0=makeQuery(id+"F11.opExtrude","SWEPT_BODY",BODY,{"disambiguationData":[OSD([sQuery(id+"F10.wireOp",EDGE,"E596.sketch_text.stroke-100"),sQuery(id+"F10.wireOp",EDGE,"E596.sketch_text.stroke-101"),sQuery(id+"F10.wireOp",EDGE,"E596.sketch_text.stroke-102"),sQuery(id+"F10.wireOp",EDGE,"E596.sketch_text.stroke-103"),sQuery(id+"F10.wireOp",EDGE,"E596.sketch_text.stroke-104"),sQuery(id+"F10.wireOp",EDGE,"E596.sketch_text.stroke-105"),sQuery(id+"F10.wireOp",EDGE,"E596.sketch_text.stroke-106"),sQuery(id+"F10.wireOp",EDGE,"E596.sketch_text.stroke-107"),sQuery(id+"F10.wireOp",EDGE,"E596.sketch_text.stroke-108"),sQuery(id+"F10.wireOp",EDGE,"E596.sketch_text.stroke-109"),sQuery(id+"F10.wireOp",EDGE,"E596.sketch_text.stroke-110"),sQuery(id+"F10.wireOp",EDGE,"E596.sketch_text.stroke-111"),sQuery(id+"F10.wireOp",EDGE,"E596.sketch_text.stroke-112"),sQuery(id+"F10.wireOp",EDGE,"E596.sketch_text.stroke-113"),sQuery(id+"F10.wireOp",EDGE,"E596.sketch_text.stroke-114"),sQuery(id+"F10.wireOp",EDGE,"E596.sketch_text.stroke-115"),sQuery(id+"F10.wireOp",EDGE,"E596.sketch_text.stroke-116"),sQuery(id+"F10.wireOp",EDGE,"E596.sketch_text.stroke-117"),sQuery(id+"F10.wireOp",EDGE,"E596.sketch_text.stroke-118"),sQuery(id+"F10.wireOp",EDGE,"E596.sketch_text.stroke-119"),sQuery(id+"F10.wireOp",EDGE,"E596.sketch_text.stroke-120"),sQuery(id+"F10.wireOp",EDGE,"E596.sketch_text.stroke-121"),sQuery(id+"F10.wireOp",EDGE,"E596.sketch_text.stroke-122"),sQuery(id+"F10.wireOp",EDGE,"E596.sketch_text.stroke-123")])]});
            transform(context, id + "F16", {"entities" : qUnion([Q0]), "transformType" : TransformType.TRANSLATION_3D, "dx" : -7.5 * mm, "dy" : 0 * mm, "dz" : 1.6 * mm, "makeCopy" : false});
        }
        {
            var Q0;
            Q0=makeQuery(id+"F11.opExtrude","SWEPT_BODY",BODY,{"disambiguationData":[OSD([sQuery(id+"F10.wireOp",EDGE,"E596.sketch_text.stroke-124"),sQuery(id+"F10.wireOp",EDGE,"E596.sketch_text.stroke-125"),sQuery(id+"F10.wireOp",EDGE,"E596.sketch_text.stroke-126"),sQuery(id+"F10.wireOp",EDGE,"E596.sketch_text.stroke-127"),sQuery(id+"F10.wireOp",EDGE,"E596.sketch_text.stroke-128"),sQuery(id+"F10.wireOp",EDGE,"E596.sketch_text.stroke-129"),sQuery(id+"F10.wireOp",EDGE,"E596.sketch_text.stroke-130"),sQuery(id+"F10.wireOp",EDGE,"E596.sketch_text.stroke-131"),sQuery(id+"F10.wireOp",EDGE,"E596.sketch_text.stroke-132"),sQuery(id+"F10.wireOp",EDGE,"E596.sketch_text.stroke-133"),sQuery(id+"F10.wireOp",EDGE,"E596.sketch_text.stroke-134"),sQuery(id+"F10.wireOp",EDGE,"E596.sketch_text.stroke-135"),sQuery(id+"F10.wireOp",EDGE,"E596.sketch_text.stroke-136"),sQuery(id+"F10.wireOp",EDGE,"E596.sketch_text.stroke-137"),sQuery(id+"F10.wireOp",EDGE,"E596.sketch_text.stroke-138"),sQuery(id+"F10.wireOp",EDGE,"E596.sketch_text.stroke-139"),sQuery(id+"F10.wireOp",EDGE,"E596.sketch_text.stroke-140"),sQuery(id+"F10.wireOp",EDGE,"E596.sketch_text.stroke-141"),sQuery(id+"F10.wireOp",EDGE,"E596.sketch_text.stroke-142"),sQuery(id+"F10.wireOp",EDGE,"E596.sketch_text.stroke-143"),sQuery(id+"F10.wireOp",EDGE,"E596.sketch_text.stroke-144"),sQuery(id+"F10.wireOp",EDGE,"E596.sketch_text.stroke-145"),sQuery(id+"F10.wireOp",EDGE,"E596.sketch_text.stroke-146"),sQuery(id+"F10.wireOp",EDGE,"E596.sketch_text.stroke-147"),sQuery(id+"F10.wireOp",EDGE,"E596.sketch_text.stroke-148"),sQuery(id+"F10.wireOp",EDGE,"E596.sketch_text.stroke-149")])]});
            transform(context, id + "F17", {"entities" : qUnion([Q0]), "transformType" : TransformType.TRANSLATION_3D, "dx" : -9 * mm, "dy" : 0 * mm, "dz" : 1.6 * mm, "makeCopy" : false});
        }
        {
            var Q0;
            Q0=makeQuery(id+"F11.opExtrude","SWEPT_BODY",BODY,{"disambiguationData":[OSD([sQuery(id+"F10.wireOp",EDGE,"E596.sketch_text.stroke-150"),sQuery(id+"F10.wireOp",EDGE,"E596.sketch_text.stroke-151"),sQuery(id+"F10.wireOp",EDGE,"E596.sketch_text.stroke-152"),sQuery(id+"F10.wireOp",EDGE,"E596.sketch_text.stroke-153"),sQuery(id+"F10.wireOp",EDGE,"E596.sketch_text.stroke-154"),sQuery(id+"F10.wireOp",EDGE,"E596.sketch_text.stroke-155"),sQuery(id+"F10.wireOp",EDGE,"E596.sketch_text.stroke-156"),sQuery(id+"F10.wireOp",EDGE,"E596.sketch_text.stroke-157"),sQuery(id+"F10.wireOp",EDGE,"E596.sketch_text.stroke-158"),sQuery(id+"F10.wireOp",EDGE,"E596.sketch_text.stroke-159"),sQuery(id+"F10.wireOp",EDGE,"E596.sketch_text.stroke-160"),sQuery(id+"F10.wireOp",EDGE,"E596.sketch_text.stroke-161"),sQuery(id+"F10.wireOp",EDGE,"E596.sketch_text.stroke-162"),sQuery(id+"F10.wireOp",EDGE,"E596.sketch_text.stroke-163"),sQuery(id+"F10.wireOp",EDGE,"E596.sketch_text.stroke-164"),sQuery(id+"F10.wireOp",EDGE,"E596.sketch_text.stroke-165")])]});
            transform(context, id + "F18", {"entities" : qUnion([Q0]), "transformType" : TransformType.TRANSLATION_3D, "dx" : -4.7 * mm, "dy" : 0 * mm, "dz" : 7.7 * mm, "makeCopy" : false});
        }
        {
            var Q0;
            Q0=makeQuery(id+"F11.opExtrude","SWEPT_BODY",BODY,{"disambiguationData":[OSD([sQuery(id+"F10.wireOp",EDGE,"E596.sketch_text.stroke-166"),sQuery(id+"F10.wireOp",EDGE,"E596.sketch_text.stroke-167"),sQuery(id+"F10.wireOp",EDGE,"E596.sketch_text.stroke-168"),sQuery(id+"F10.wireOp",EDGE,"E596.sketch_text.stroke-169"),sQuery(id+"F10.wireOp",EDGE,"E596.sketch_text.stroke-170"),sQuery(id+"F10.wireOp",EDGE,"E596.sketch_text.stroke-171"),sQuery(id+"F10.wireOp",EDGE,"E596.sketch_text.stroke-172"),sQuery(id+"F10.wireOp",EDGE,"E596.sketch_text.stroke-173"),sQuery(id+"F10.wireOp",EDGE,"E596.sketch_text.stroke-174"),sQuery(id+"F10.wireOp",EDGE,"E596.sketch_text.stroke-175"),sQuery(id+"F10.wireOp",EDGE,"E596.sketch_text.stroke-176"),sQuery(id+"F10.wireOp",EDGE,"E596.sketch_text.stroke-177"),sQuery(id+"F10.wireOp",EDGE,"E596.sketch_text.stroke-178"),sQuery(id+"F10.wireOp",EDGE,"E596.sketch_text.stroke-179"),sQuery(id+"F10.wireOp",EDGE,"E596.sketch_text.stroke-180"),sQuery(id+"F10.wireOp",EDGE,"E596.sketch_text.stroke-181"),sQuery(id+"F10.wireOp",EDGE,"E596.sketch_text.stroke-182"),sQuery(id+"F10.wireOp",EDGE,"E596.sketch_text.stroke-183"),sQuery(id+"F10.wireOp",EDGE,"E596.sketch_text.stroke-184"),sQuery(id+"F10.wireOp",EDGE,"E596.sketch_text.stroke-185"),sQuery(id+"F10.wireOp",EDGE,"E596.sketch_text.stroke-186"),sQuery(id+"F10.wireOp",EDGE,"E596.sketch_text.stroke-187"),sQuery(id+"F10.wireOp",EDGE,"E596.sketch_text.stroke-188"),sQuery(id+"F10.wireOp",EDGE,"E596.sketch_text.stroke-189")])]});
            transform(context, id + "F19", {"entities" : qUnion([Q0]), "transformType" : TransformType.TRANSLATION_3D, "dx" : -5.9 * mm, "dy" : 0 * mm, "dz" : 7.3 * mm, "makeCopy" : false});
        }
        {
            var Q0;
            Q0=makeQuery(id+"F11.opExtrude","SWEPT_BODY",BODY,{"disambiguationData":[OSD([sQuery(id+"F10.wireOp",EDGE,"E596.sketch_text.stroke-190"),sQuery(id+"F10.wireOp",EDGE,"E596.sketch_text.stroke-191"),sQuery(id+"F10.wireOp",EDGE,"E596.sketch_text.stroke-192"),sQuery(id+"F10.wireOp",EDGE,"E596.sketch_text.stroke-193"),sQuery(id+"F10.wireOp",EDGE,"E596.sketch_text.stroke-194"),sQuery(id+"F10.wireOp",EDGE,"E596.sketch_text.stroke-195"),sQuery(id+"F10.wireOp",EDGE,"E596.sketch_text.stroke-196"),sQuery(id+"F10.wireOp",EDGE,"E596.sketch_text.stroke-197"),sQuery(id+"F10.wireOp",EDGE,"E596.sketch_text.stroke-198"),sQuery(id+"F10.wireOp",EDGE,"E596.sketch_text.stroke-199"),sQuery(id+"F10.wireOp",EDGE,"E596.sketch_text.stroke-200"),sQuery(id+"F10.wireOp",EDGE,"E596.sketch_text.stroke-201"),sQuery(id+"F10.wireOp",EDGE,"E596.sketch_text.stroke-202"),sQuery(id+"F10.wireOp",EDGE,"E596.sketch_text.stroke-203"),sQuery(id+"F10.wireOp",EDGE,"E596.sketch_text.stroke-204"),sQuery(id+"F10.wireOp",EDGE,"E596.sketch_text.stroke-205"),sQuery(id+"F10.wireOp",EDGE,"E596.sketch_text.stroke-206"),sQuery(id+"F10.wireOp",EDGE,"E596.sketch_text.stroke-207"),sQuery(id+"F10.wireOp",EDGE,"E596.sketch_text.stroke-208"),sQuery(id+"F10.wireOp",EDGE,"E596.sketch_text.stroke-209"),sQuery(id+"F10.wireOp",EDGE,"E596.sketch_text.stroke-210"),sQuery(id+"F10.wireOp",EDGE,"E596.sketch_text.stroke-211"),sQuery(id+"F10.wireOp",EDGE,"E596.sketch_text.stroke-212"),sQuery(id+"F10.wireOp",EDGE,"E596.sketch_text.stroke-213"),sQuery(id+"F10.wireOp",EDGE,"E596.sketch_text.stroke-214"),sQuery(id+"F10.wireOp",EDGE,"E596.sketch_text.stroke-215"),sQuery(id+"F10.wireOp",EDGE,"E596.sketch_text.stroke-216"),sQuery(id+"F10.wireOp",EDGE,"E596.sketch_text.stroke-217"),sQuery(id+"F10.wireOp",EDGE,"E596.sketch_text.stroke-218"),sQuery(id+"F10.wireOp",EDGE,"E596.sketch_text.stroke-219"),sQuery(id+"F10.wireOp",EDGE,"E596.sketch_text.stroke-220"),sQuery(id+"F10.wireOp",EDGE,"E596.sketch_text.stroke-221")])]});
            transform(context, id + "F20", {"entities" : qUnion([Q0]), "transformType" : TransformType.TRANSLATION_3D, "dx" : -7.3 * mm, "dy" : 0 * mm, "dz" : 9.3 * mm, "makeCopy" : false});
        }
        {
            var Q0;
            Q0=makeQuery(id+"F11.opExtrude","SWEPT_BODY",BODY,{"disambiguationData":[OSD([sQuery(id+"F10.wireOp",EDGE,"E596.sketch_text.stroke-222"),sQuery(id+"F10.wireOp",EDGE,"E596.sketch_text.stroke-223"),sQuery(id+"F10.wireOp",EDGE,"E596.sketch_text.stroke-224"),sQuery(id+"F10.wireOp",EDGE,"E596.sketch_text.stroke-225"),sQuery(id+"F10.wireOp",EDGE,"E596.sketch_text.stroke-226"),sQuery(id+"F10.wireOp",EDGE,"E596.sketch_text.stroke-227"),sQuery(id+"F10.wireOp",EDGE,"E596.sketch_text.stroke-228"),sQuery(id+"F10.wireOp",EDGE,"E596.sketch_text.stroke-229"),sQuery(id+"F10.wireOp",EDGE,"E596.sketch_text.stroke-230"),sQuery(id+"F10.wireOp",EDGE,"E596.sketch_text.stroke-231"),sQuery(id+"F10.wireOp",EDGE,"E596.sketch_text.stroke-232"),sQuery(id+"F10.wireOp",EDGE,"E596.sketch_text.stroke-233"),sQuery(id+"F10.wireOp",EDGE,"E596.sketch_text.stroke-234"),sQuery(id+"F10.wireOp",EDGE,"E596.sketch_text.stroke-235"),sQuery(id+"F10.wireOp",EDGE,"E596.sketch_text.stroke-236"),sQuery(id+"F10.wireOp",EDGE,"E596.sketch_text.stroke-237"),sQuery(id+"F10.wireOp",EDGE,"E596.sketch_text.stroke-238"),sQuery(id+"F10.wireOp",EDGE,"E596.sketch_text.stroke-239"),sQuery(id+"F10.wireOp",EDGE,"E596.sketch_text.stroke-240"),sQuery(id+"F10.wireOp",EDGE,"E596.sketch_text.stroke-241"),sQuery(id+"F10.wireOp",EDGE,"E596.sketch_text.stroke-242"),sQuery(id+"F10.wireOp",EDGE,"E596.sketch_text.stroke-243"),sQuery(id+"F10.wireOp",EDGE,"E596.sketch_text.stroke-244"),sQuery(id+"F10.wireOp",EDGE,"E596.sketch_text.stroke-245")])]});
            transform(context, id + "F21", {"entities" : qUnion([Q0]), "transformType" : TransformType.TRANSLATION_3D, "dx" : -8.5 * mm, "dy" : 0 * mm, "dz" : 7.4 * mm, "makeCopy" : false});
        }
        {
            var Q0;
            Q0=makeQuery(id+"F11.opExtrude","SWEPT_BODY",BODY,{"disambiguationData":[OSD([sQuery(id+"F10.wireOp",EDGE,"E596.sketch_text.stroke-246"),sQuery(id+"F10.wireOp",EDGE,"E596.sketch_text.stroke-247"),sQuery(id+"F10.wireOp",EDGE,"E596.sketch_text.stroke-248"),sQuery(id+"F10.wireOp",EDGE,"E596.sketch_text.stroke-249"),sQuery(id+"F10.wireOp",EDGE,"E596.sketch_text.stroke-250"),sQuery(id+"F10.wireOp",EDGE,"E596.sketch_text.stroke-251"),sQuery(id+"F10.wireOp",EDGE,"E596.sketch_text.stroke-252"),sQuery(id+"F10.wireOp",EDGE,"E596.sketch_text.stroke-253"),sQuery(id+"F10.wireOp",EDGE,"E596.sketch_text.stroke-254"),sQuery(id+"F10.wireOp",EDGE,"E596.sketch_text.stroke-255"),sQuery(id+"F10.wireOp",EDGE,"E596.sketch_text.stroke-256"),sQuery(id+"F10.wireOp",EDGE,"E596.sketch_text.stroke-257"),sQuery(id+"F10.wireOp",EDGE,"E596.sketch_text.stroke-258"),sQuery(id+"F10.wireOp",EDGE,"E596.sketch_text.stroke-259"),sQuery(id+"F10.wireOp",EDGE,"E596.sketch_text.stroke-260"),sQuery(id+"F10.wireOp",EDGE,"E596.sketch_text.stroke-261"),sQuery(id+"F10.wireOp",EDGE,"E596.sketch_text.stroke-262"),sQuery(id+"F10.wireOp",EDGE,"E596.sketch_text.stroke-263"),sQuery(id+"F10.wireOp",EDGE,"E596.sketch_text.stroke-264"),sQuery(id+"F10.wireOp",EDGE,"E596.sketch_text.stroke-265"),sQuery(id+"F10.wireOp",EDGE,"E596.sketch_text.stroke-266"),sQuery(id+"F10.wireOp",EDGE,"E596.sketch_text.stroke-267"),sQuery(id+"F10.wireOp",EDGE,"E596.sketch_text.stroke-268"),sQuery(id+"F10.wireOp",EDGE,"E596.sketch_text.stroke-269"),sQuery(id+"F10.wireOp",EDGE,"E596.sketch_text.stroke-270"),sQuery(id+"F10.wireOp",EDGE,"E596.sketch_text.stroke-271")])]});
            var Q1;
            Q1=makeQuery(id+"F11.opExtrude","SWEPT_BODY",BODY,{"disambiguationData":[OSD([sQuery(id+"F10.wireOp",EDGE,"E596.sketch_text.stroke-272"),sQuery(id+"F10.wireOp",EDGE,"E596.sketch_text.stroke-273"),sQuery(id+"F10.wireOp",EDGE,"E596.sketch_text.stroke-274"),sQuery(id+"F10.wireOp",EDGE,"E596.sketch_text.stroke-275"),sQuery(id+"F10.wireOp",EDGE,"E596.sketch_text.stroke-276"),sQuery(id+"F10.wireOp",EDGE,"E596.sketch_text.stroke-277"),sQuery(id+"F10.wireOp",EDGE,"E596.sketch_text.stroke-278"),sQuery(id+"F10.wireOp",EDGE,"E596.sketch_text.stroke-279"),sQuery(id+"F10.wireOp",EDGE,"E596.sketch_text.stroke-280"),sQuery(id+"F10.wireOp",EDGE,"E596.sketch_text.stroke-281"),sQuery(id+"F10.wireOp",EDGE,"E596.sketch_text.stroke-282"),sQuery(id+"F10.wireOp",EDGE,"E596.sketch_text.stroke-283"),sQuery(id+"F10.wireOp",EDGE,"E596.sketch_text.stroke-284"),sQuery(id+"F10.wireOp",EDGE,"E596.sketch_text.stroke-285"),sQuery(id+"F10.wireOp",EDGE,"E596.sketch_text.stroke-286"),sQuery(id+"F10.wireOp",EDGE,"E596.sketch_text.stroke-287"),sQuery(id+"F10.wireOp",EDGE,"E596.sketch_text.stroke-288"),sQuery(id+"F10.wireOp",EDGE,"E596.sketch_text.stroke-289"),sQuery(id+"F10.wireOp",EDGE,"E596.sketch_text.stroke-290"),sQuery(id+"F10.wireOp",EDGE,"E596.sketch_text.stroke-291"),sQuery(id+"F10.wireOp",EDGE,"E596.sketch_text.stroke-292"),sQuery(id+"F10.wireOp",EDGE,"E596.sketch_text.stroke-293"),sQuery(id+"F10.wireOp",EDGE,"E596.sketch_text.stroke-294"),sQuery(id+"F10.wireOp",EDGE,"E596.sketch_text.stroke-295"),sQuery(id+"F10.wireOp",EDGE,"E596.sketch_text.stroke-296"),sQuery(id+"F10.wireOp",EDGE,"E596.sketch_text.stroke-297"),sQuery(id+"F10.wireOp",EDGE,"E596.sketch_text.stroke-298"),sQuery(id+"F10.wireOp",EDGE,"E596.sketch_text.stroke-299"),sQuery(id+"F10.wireOp",EDGE,"E596.sketch_text.stroke-300")])]});
            transform(context, id + "F22", {"entities" : qUnion([Q0, Q1]), "transformType" : TransformType.TRANSLATION_3D, "dx" : -9.8 * mm, "dy" : 0 * mm, "dz" : 7.3 * mm, "makeCopy" : false});
        }
        {
            var Q0;
            Q0=makeQuery(id+"F11.opExtrude","SWEPT_BODY",BODY,{"disambiguationData":[OSD([sQuery(id+"F10.wireOp",EDGE,"E596.sketch_text.stroke-272"),sQuery(id+"F10.wireOp",EDGE,"E596.sketch_text.stroke-273"),sQuery(id+"F10.wireOp",EDGE,"E596.sketch_text.stroke-274"),sQuery(id+"F10.wireOp",EDGE,"E596.sketch_text.stroke-275"),sQuery(id+"F10.wireOp",EDGE,"E596.sketch_text.stroke-276"),sQuery(id+"F10.wireOp",EDGE,"E596.sketch_text.stroke-277"),sQuery(id+"F10.wireOp",EDGE,"E596.sketch_text.stroke-278"),sQuery(id+"F10.wireOp",EDGE,"E596.sketch_text.stroke-279"),sQuery(id+"F10.wireOp",EDGE,"E596.sketch_text.stroke-280"),sQuery(id+"F10.wireOp",EDGE,"E596.sketch_text.stroke-281"),sQuery(id+"F10.wireOp",EDGE,"E596.sketch_text.stroke-282"),sQuery(id+"F10.wireOp",EDGE,"E596.sketch_text.stroke-283"),sQuery(id+"F10.wireOp",EDGE,"E596.sketch_text.stroke-284"),sQuery(id+"F10.wireOp",EDGE,"E596.sketch_text.stroke-285"),sQuery(id+"F10.wireOp",EDGE,"E596.sketch_text.stroke-286"),sQuery(id+"F10.wireOp",EDGE,"E596.sketch_text.stroke-287"),sQuery(id+"F10.wireOp",EDGE,"E596.sketch_text.stroke-288"),sQuery(id+"F10.wireOp",EDGE,"E596.sketch_text.stroke-289"),sQuery(id+"F10.wireOp",EDGE,"E596.sketch_text.stroke-290"),sQuery(id+"F10.wireOp",EDGE,"E596.sketch_text.stroke-291"),sQuery(id+"F10.wireOp",EDGE,"E596.sketch_text.stroke-292"),sQuery(id+"F10.wireOp",EDGE,"E596.sketch_text.stroke-293"),sQuery(id+"F10.wireOp",EDGE,"E596.sketch_text.stroke-294"),sQuery(id+"F10.wireOp",EDGE,"E596.sketch_text.stroke-295"),sQuery(id+"F10.wireOp",EDGE,"E596.sketch_text.stroke-296"),sQuery(id+"F10.wireOp",EDGE,"E596.sketch_text.stroke-297"),sQuery(id+"F10.wireOp",EDGE,"E596.sketch_text.stroke-298"),sQuery(id+"F10.wireOp",EDGE,"E596.sketch_text.stroke-299"),sQuery(id+"F10.wireOp",EDGE,"E596.sketch_text.stroke-300")])]});
            transform(context, id + "F23", {"entities" : qUnion([Q0]), "transformType" : TransformType.TRANSLATION_3D, "dx" : -1.2 * mm, "dy" : 0 * mm, "dz" : 0 * mm, "makeCopy" : false});
        }
        {
            var Q0;
            Q0=qCreatedBy(makeId("Front.planeOp"),FACE);
            var sketch = newSketch(context, id + "F24", { "sketchPlane" : qUnion([Q0])});
            skLineSegment(sketch, "E597.bottom", {"start": v(-78.2, 4.26) * mm, "end": v(61.5, 4.26) * mm});
            skLineSegment(sketch, "E597.top", {"start": v(-78.2, 0.56) * mm, "end": v(61.5, 0.56) * mm});
            skLineSegment(sketch, "E597.left", {"start": v(-78.2, 4.26) * mm, "end": v(-78.2, 0.56) * mm});
            skLineSegment(sketch, "E597.right", {"start": v(61.5, 4.26) * mm, "end": v(61.5, 0.56) * mm});
            skSolve(sketch);
        }
        {
            var Q0;
            Q0 = qSketchRegion(id + "F24", true);
            extrude(context, id + "F25", {"entities" : qUnion([Q0]), "depth" : 9.7 * mm, "offsetDistance" : 25 * mm});
        }
        {
            var Q0;
            Q0=makeQuery(id+"F25.opExtrude","CAP_EDGE",EDGE,{"disambiguationData":[OSD([sQuery(id+"F24.wireOp",EDGE,"E597.top")])],"isStart":false});
            chamfer(context, id + "F26", {"entities" : qUnion([Q0]), "width" : 4 * mm, "tangentPropagation" : true});
        }
    });
